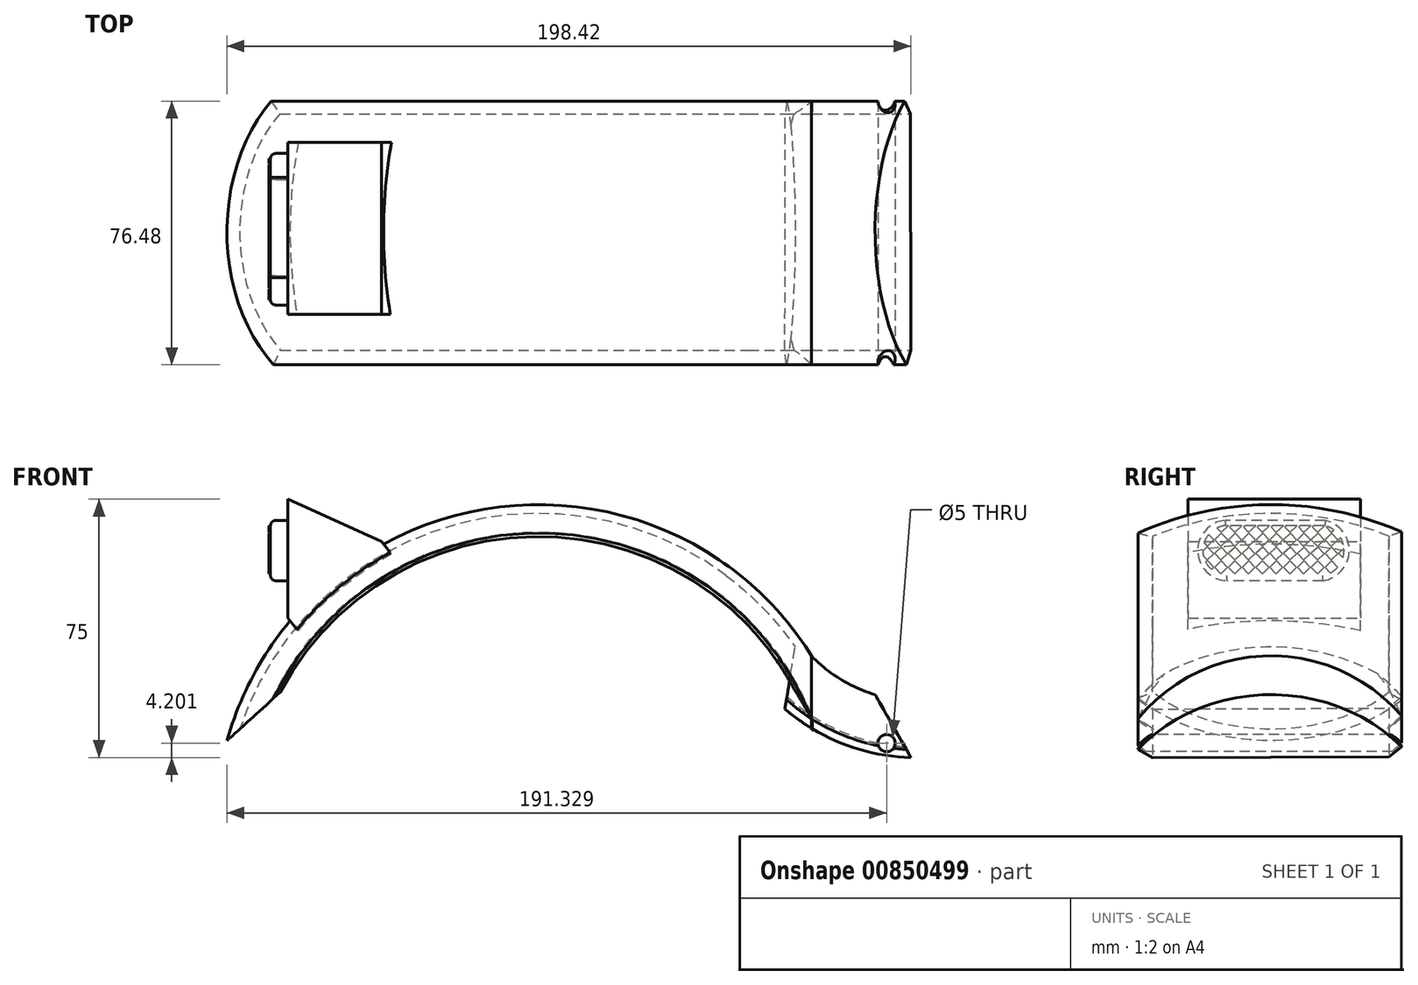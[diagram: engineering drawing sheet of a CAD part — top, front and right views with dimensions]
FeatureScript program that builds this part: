
annotation { "Feature Type Name" : "Feature", "Feature Type Description" : "" }
export const myFeature = defineFeature(function(context is Context, id is Id, definition is map)
    precondition{}
    {
        {
            var Q0;
            Q0=qCreatedBy(makeId("Front.planeOp"),FACE);
            var sketch = newSketch(context, id + "F0", { "sketchPlane" : qUnion([Q0])});
            skFitSpline(sketch, "E0", {"points": [v(68.37, 41.54) * mm, v(83.67, 28.77) * mm, v(119.21, 26.3) * mm], "startDerivative": vector(22.7, -35.07) * mm, "endDerivative": vector(68.28, -4.16) * mm});
            skLineSegment(sketch, "E1", {"start": v(68.5, 41.4) * mm, "end": v(68.47, 41.39) * mm});
            skArc(sketch, "E2.trimOffspring", {"start": v(68.5, 41.4) * mm, "mid": v(68.43, 41.47) * mm, "end": v(68.37, 41.54) * mm});
            skArc(sketch, "E3", {"start": v(68.5, 41.4) * mm, "mid": v(68.45, 41.44) * mm, "end": v(68.4, 41.48) * mm});
            skArc(sketch, "E4", {"start": v(68.37, 41.54) * mm, "mid": v(54.41, 56.97) * mm, "end": v(37.54, 69.12) * mm});
            skArc(sketch, "E5", {"start": v(37.54, 69.12) * mm, "mid": v(-52.48, 72.9) * mm, "end": v(-108.29, 2.17) * mm});
            skPoint(sketch, "E6.orphan", {"position": v(71.6, 37.23) * mm});
            skArc(sketch, "E7", {"start": v(68.4, 41.48) * mm, "mid": v(77.01, 32.62) * mm, "end": v(88.08, 27.14) * mm});
            skSolve(sketch);
        }
        {
            var Q0;
            Q0=qCreatedBy(makeId("Right.planeOp"),FACE);
            cPlane(context, id + "F1", {"entities" : qUnion([Q0]), "cplaneType" : CPlaneType.OFFSET, "offset" : 68 * mm, "width" : 150 * mm, "height" : 150 * mm});
        }
        {
            var Q0;
            Q0=qCreatedBy(id+"F1.planeOp",FACE);
            var sketch = newSketch(context, id + "F2", { "sketchPlane" : qUnion([Q0])});
            skArc(sketch, "E8", {"start": v(36.9, 15.62) * mm, "mid": v(-1.55, 32.94) * mm, "end": v(-39.57, 14.68) * mm});
            skArc(sketch, "E9.0", {"start": v(33.28, 12.17) * mm, "mid": v(-1.1, 27.94) * mm, "end": v(-35.37, 11.91) * mm});
            skLineSegment(sketch, "E10", {"start": v(-39.57, 14.68) * mm, "end": v(-35.37, 11.91) * mm});
            skLineSegment(sketch, "E11", {"start": v(36.9, 15.62) * mm, "end": v(33.28, 12.17) * mm});
            skLineSegment(sketch, "E12", {"start": v(-35.37, 11.91) * mm, "end": v(33.28, 12.17) * mm});
            skSolve(sketch);
        }
        {
            var Q0;
            Q0=makeQuery(id+"F2.imprint","IMPRINT",FACE,{"disambiguationData":[TD([[makeQuery(id+"F2.imprint","IMPRINT",EDGE,{"derivedFrom":sQuery(id+"F2.wireOp",EDGE,"E8")}),1.0]])]});
            var Q1;
            Q1=sQuery(id+"F0.wireOp",EDGE,"E4");
            var Q2;
            Q2=sQuery(id+"F0.wireOp",EDGE,"E5");
            sweep(context, id + "F3", {"profiles" : qUnion([Q0]), "path" : qUnion([Q1, Q2])});
        }
        {
            var Q0;
            Q0 = qSketchRegion(id + "F2", true);
            var Q1;
            Q1=sQuery(id+"F0.wireOp",EDGE,"E7");
            sweep(context, id + "F4", {"operationType" : NewBodyOperationType.ADD, "profiles" : qUnion([Q0]), "path" : qUnion([Q1])});
        }
        {
            var Q0;
            Q0=qCreatedBy(makeId("Front.planeOp"),FACE);
            var sketch = newSketch(context, id + "F5", { "sketchPlane" : qUnion([Q0])});
            skCircle(sketch, "E13", {"center": v(89.77, 7.6) * mm, "radius": 2.5 * mm});
            skSolve(sketch);
        }
        {
            var Q0;
            Q0 = qSketchRegion(id + "F5", true);
            extrude(context, id + "F6", {"entities" : qUnion([Q0]), "operationType" : NewBodyOperationType.REMOVE, "oppositeDirection" : true, "depth" : 100 * mm, "offsetDistance" : 25 * mm, "symmetric" : true});
        }
        {
            var Q0;
            Q0=qCreatedBy(makeId("Front.planeOp"),FACE);
            var sketch = newSketch(context, id + "F7", { "sketchPlane" : qUnion([Q0])});
            skLineSegment(sketch, "E14", {"start": v(-83.93, 78.4) * mm, "end": v(-83.93, 43.94) * mm});
            skLineSegment(sketch, "E15", {"start": v(-83.93, 78.4) * mm, "end": v(-56.75, 66.07) * mm});
            skLineSegment(sketch, "E16", {"start": v(-56.75, 66.07) * mm, "end": v(-83.93, 43.94) * mm});
            skSolve(sketch);
        }
        {
            var Q0;
            Q0=makeQuery(id+"F7.imprint","IMPRINT",FACE,{"disambiguationData":[TD([[makeQuery(id+"F7.imprint","IMPRINT",EDGE,{"derivedFrom":sQuery(id+"F7.wireOp",EDGE,"E14")}),1.0]])]});
            extrude(context, id + "F8", {"entities" : qUnion([Q0]), "operationType" : NewBodyOperationType.ADD, "depth" : 50 * mm, "offsetDistance" : 25 * mm, "symmetric" : true});
        }
        {
            var Q0;
            Q0=makeQuery(id+"F8.opExtrude","SWEPT_FACE",FACE,{"disambiguationData":[OSD([sQuery(id+"F7.wireOp",EDGE,"E16")])]});
            extrude(context, id + "F9", {"entities" : qUnion([Q0]), "operationType" : NewBodyOperationType.ADD, "endBound" : BoundingType.UP_TO_NEXT, "depth" : 25 * mm, "offsetDistance" : 25 * mm});
        }
        {
            var Q0;
            Q0=makeQuery(id+"F8.opExtrude","SWEPT_FACE",FACE,{"disambiguationData":[OSD([sQuery(id+"F7.wireOp",EDGE,"E14")])]});
            var sketch = newSketch(context, id + "F10", { "sketchPlane" : qUnion([Q0])});
            skLineSegment(sketch, "E17.bottom", {"start": v(-14.83, 72.23) * mm, "end": v(14.26, 72.23) * mm});
            skLineSegment(sketch, "E17.top", {"start": v(-14.17, 54.73) * mm, "end": v(13.78, 54.73) * mm});
            skArc(sketch, "E18", {"start": v(-14.83, 72.23) * mm, "mid": v(-21.73, 63.2) * mm, "end": v(-14.17, 54.73) * mm});
            skArc(sketch, "E19", {"start": v(13.78, 54.73) * mm, "mid": v(22.21, 63.26) * mm, "end": v(14.26, 72.23) * mm});
            skSolve(sketch);
        }
        {
            var Q0;
            Q0 = qSketchRegion(id + "F10", true);
            extrude(context, id + "F11", {"entities" : qUnion([Q0]), "depth" : 5 * mm, "offsetDistance" : 25 * mm});
        }
        {
            var Q0;
            Q0=makeQuery(id+"F11.opExtrude","CAP_EDGE",EDGE,{"disambiguationData":[OSD([sQuery(id+"F10.wireOp",EDGE,"E18")])],"isStart":false});
            var Q1;
            Q1=makeQuery(id+"F11.opExtrude","CAP_EDGE",EDGE,{"disambiguationData":[OSD([sQuery(id+"F10.wireOp",EDGE,"E17.bottom")])],"isStart":false});
            var Q2;
            Q2=makeQuery(id+"F11.opExtrude","CAP_FACE",FACE,{"disambiguationData":[OSD([sQuery(id+"F10.wireOp",EDGE,"E17.bottom"),sQuery(id+"F10.wireOp",EDGE,"E17.top"),sQuery(id+"F10.wireOp",EDGE,"E18"),sQuery(id+"F10.wireOp",EDGE,"E19")])],"isStart":false});
            fillet(context, id + "F12", {"entities" : qUnion([Q0, Q1, Q2]), "radius" : 1.5 * mm, "tangentPropagation" : true, "allowEdgeOverflow" : false});
        }
        {
            var Q0;
            Q0=makeQuery(id+"F11.opExtrude","CAP_FACE",FACE,{"disambiguationData":[OSD([sQuery(id+"F10.wireOp",EDGE,"E17.bottom"),sQuery(id+"F10.wireOp",EDGE,"E17.top"),sQuery(id+"F10.wireOp",EDGE,"E18"),sQuery(id+"F10.wireOp",EDGE,"E19")])],"isStart":false});
            var sketch = newSketch(context, id + "F13", { "sketchPlane" : qUnion([Q0])});
            skLineSegment(sketch, "E20", {"start": v(-14.65, 70.73) * mm, "end": v(-16.72, 68.56) * mm});
            skLineSegment(sketch, "E21", {"start": v(-16.72, 68.56) * mm, "end": v(-14.55, 66.49) * mm});
            skLineSegment(sketch, "E22", {"start": v(-14.55, 66.49) * mm, "end": v(-12.48, 68.66) * mm});
            skLineSegment(sketch, "E23", {"start": v(-12.48, 68.66) * mm, "end": v(-14.65, 70.73) * mm});
            skLineSegment(sketch, "E24.0", {"start": v(-16.01, 68.58) * mm, "end": v(-14.57, 67.2) * mm});
            skLineSegment(sketch, "E25.0", {"start": v(-14.63, 70.02) * mm, "end": v(-16.01, 68.58) * mm});
            skLineSegment(sketch, "E26.0", {"start": v(-13.19, 68.64) * mm, "end": v(-14.63, 70.02) * mm});
            skLineSegment(sketch, "E27.0", {"start": v(-14.57, 67.2) * mm, "end": v(-13.19, 68.64) * mm});
            skLineSegment(sketch, "E28.1.0.0", {"start": v(-10.65, 70.73) * mm, "end": v(-12.72, 68.56) * mm});
            skLineSegment(sketch, "E28.1.0.1", {"start": v(-10.63, 70.02) * mm, "end": v(-12.01, 68.58) * mm});
            skLineSegment(sketch, "E28.1.0.2", {"start": v(-9.19, 68.64) * mm, "end": v(-10.63, 70.02) * mm});
            skLineSegment(sketch, "E28.1.0.3", {"start": v(-8.48, 68.66) * mm, "end": v(-10.65, 70.73) * mm});
            skLineSegment(sketch, "E28.1.0.4", {"start": v(-10.55, 66.49) * mm, "end": v(-8.48, 68.66) * mm});
            skLineSegment(sketch, "E28.1.0.5", {"start": v(-10.57, 67.2) * mm, "end": v(-9.19, 68.64) * mm});
            skLineSegment(sketch, "E28.1.0.6", {"start": v(-12.01, 68.58) * mm, "end": v(-10.57, 67.2) * mm});
            skLineSegment(sketch, "E28.1.0.7", {"start": v(-12.72, 68.56) * mm, "end": v(-10.55, 66.49) * mm});
            skLineSegment(sketch, "E28.2.0.0", {"start": v(-6.65, 70.73) * mm, "end": v(-8.72, 68.56) * mm});
            skLineSegment(sketch, "E28.2.0.1", {"start": v(-6.63, 70.02) * mm, "end": v(-8.01, 68.58) * mm});
            skLineSegment(sketch, "E28.2.0.2", {"start": v(-5.19, 68.64) * mm, "end": v(-6.63, 70.02) * mm});
            skLineSegment(sketch, "E28.2.0.3", {"start": v(-4.48, 68.66) * mm, "end": v(-6.65, 70.73) * mm});
            skLineSegment(sketch, "E28.2.0.4", {"start": v(-6.55, 66.49) * mm, "end": v(-4.48, 68.66) * mm});
            skLineSegment(sketch, "E28.2.0.5", {"start": v(-6.57, 67.2) * mm, "end": v(-5.19, 68.64) * mm});
            skLineSegment(sketch, "E28.2.0.6", {"start": v(-8.01, 68.58) * mm, "end": v(-6.57, 67.2) * mm});
            skLineSegment(sketch, "E28.2.0.7", {"start": v(-8.72, 68.56) * mm, "end": v(-6.55, 66.49) * mm});
            skLineSegment(sketch, "E28.3.0.0", {"start": v(-2.65, 70.73) * mm, "end": v(-4.72, 68.56) * mm});
            skLineSegment(sketch, "E28.3.0.1", {"start": v(-2.63, 70.02) * mm, "end": v(-4.01, 68.58) * mm});
            skLineSegment(sketch, "E28.3.0.2", {"start": v(-1.19, 68.64) * mm, "end": v(-2.63, 70.02) * mm});
            skLineSegment(sketch, "E28.3.0.3", {"start": v(-0.48, 68.66) * mm, "end": v(-2.65, 70.73) * mm});
            skLineSegment(sketch, "E28.3.0.4", {"start": v(-2.55, 66.49) * mm, "end": v(-0.48, 68.66) * mm});
            skLineSegment(sketch, "E28.3.0.5", {"start": v(-2.57, 67.2) * mm, "end": v(-1.19, 68.64) * mm});
            skLineSegment(sketch, "E28.3.0.6", {"start": v(-4.01, 68.58) * mm, "end": v(-2.57, 67.2) * mm});
            skLineSegment(sketch, "E28.3.0.7", {"start": v(-4.72, 68.56) * mm, "end": v(-2.55, 66.49) * mm});
            skLineSegment(sketch, "E28.4.0.0", {"start": v(1.35, 70.73) * mm, "end": v(-0.72, 68.56) * mm});
            skLineSegment(sketch, "E28.4.0.1", {"start": v(1.37, 70.02) * mm, "end": v(-0.01, 68.58) * mm});
            skLineSegment(sketch, "E28.4.0.2", {"start": v(2.81, 68.64) * mm, "end": v(1.37, 70.02) * mm});
            skLineSegment(sketch, "E28.4.0.3", {"start": v(3.52, 68.66) * mm, "end": v(1.35, 70.73) * mm});
            skLineSegment(sketch, "E28.4.0.4", {"start": v(1.45, 66.49) * mm, "end": v(3.52, 68.66) * mm});
            skLineSegment(sketch, "E28.4.0.5", {"start": v(1.43, 67.2) * mm, "end": v(2.81, 68.64) * mm});
            skLineSegment(sketch, "E28.4.0.6", {"start": v(-0.01, 68.58) * mm, "end": v(1.43, 67.2) * mm});
            skLineSegment(sketch, "E28.4.0.7", {"start": v(-0.72, 68.56) * mm, "end": v(1.45, 66.49) * mm});
            skLineSegment(sketch, "E28.5.0.0", {"start": v(5.35, 70.73) * mm, "end": v(3.28, 68.56) * mm});
            skLineSegment(sketch, "E28.5.0.1", {"start": v(5.37, 70.02) * mm, "end": v(3.99, 68.58) * mm});
            skLineSegment(sketch, "E28.5.0.2", {"start": v(6.81, 68.64) * mm, "end": v(5.37, 70.02) * mm});
            skLineSegment(sketch, "E28.5.0.3", {"start": v(7.52, 68.66) * mm, "end": v(5.35, 70.73) * mm});
            skLineSegment(sketch, "E28.5.0.4", {"start": v(5.45, 66.49) * mm, "end": v(7.52, 68.66) * mm});
            skLineSegment(sketch, "E28.5.0.5", {"start": v(5.43, 67.2) * mm, "end": v(6.81, 68.64) * mm});
            skLineSegment(sketch, "E28.5.0.6", {"start": v(3.99, 68.58) * mm, "end": v(5.43, 67.2) * mm});
            skLineSegment(sketch, "E28.5.0.7", {"start": v(3.28, 68.56) * mm, "end": v(5.45, 66.49) * mm});
            skLineSegment(sketch, "E28.6.0.0", {"start": v(9.35, 70.73) * mm, "end": v(7.28, 68.56) * mm});
            skLineSegment(sketch, "E28.6.0.1", {"start": v(9.37, 70.02) * mm, "end": v(7.99, 68.58) * mm});
            skLineSegment(sketch, "E28.6.0.2", {"start": v(10.81, 68.64) * mm, "end": v(9.37, 70.02) * mm});
            skLineSegment(sketch, "E28.6.0.3", {"start": v(11.52, 68.66) * mm, "end": v(9.35, 70.73) * mm});
            skLineSegment(sketch, "E28.6.0.4", {"start": v(9.45, 66.49) * mm, "end": v(11.52, 68.66) * mm});
            skLineSegment(sketch, "E28.6.0.5", {"start": v(9.43, 67.2) * mm, "end": v(10.81, 68.64) * mm});
            skLineSegment(sketch, "E28.6.0.6", {"start": v(7.99, 68.58) * mm, "end": v(9.43, 67.2) * mm});
            skLineSegment(sketch, "E28.6.0.7", {"start": v(7.28, 68.56) * mm, "end": v(9.45, 66.49) * mm});
            skLineSegment(sketch, "E28.7.0.0", {"start": v(13.35, 70.73) * mm, "end": v(11.28, 68.56) * mm});
            skLineSegment(sketch, "E28.7.0.1", {"start": v(13.37, 70.02) * mm, "end": v(11.99, 68.58) * mm});
            skLineSegment(sketch, "E28.7.0.2", {"start": v(14.81, 68.64) * mm, "end": v(13.37, 70.02) * mm});
            skLineSegment(sketch, "E28.7.0.3", {"start": v(15.52, 68.66) * mm, "end": v(13.35, 70.73) * mm});
            skLineSegment(sketch, "E28.7.0.4", {"start": v(13.45, 66.49) * mm, "end": v(15.52, 68.66) * mm});
            skLineSegment(sketch, "E28.7.0.5", {"start": v(13.43, 67.2) * mm, "end": v(14.81, 68.64) * mm});
            skLineSegment(sketch, "E28.7.0.6", {"start": v(11.99, 68.58) * mm, "end": v(13.43, 67.2) * mm});
            skLineSegment(sketch, "E28.7.0.7", {"start": v(11.28, 68.56) * mm, "end": v(13.45, 66.49) * mm});
            skLineSegment(sketch, "E28.8.0.0", {"start": v(17.35, 70.73) * mm, "end": v(15.28, 68.56) * mm});
            skLineSegment(sketch, "E28.8.0.1", {"start": v(17.37, 70.02) * mm, "end": v(15.99, 68.58) * mm});
            skLineSegment(sketch, "E28.8.0.2", {"start": v(18.81, 68.64) * mm, "end": v(17.37, 70.02) * mm});
            skLineSegment(sketch, "E28.8.0.3", {"start": v(19.52, 68.66) * mm, "end": v(17.35, 70.73) * mm});
            skLineSegment(sketch, "E28.8.0.4", {"start": v(17.45, 66.49) * mm, "end": v(19.52, 68.66) * mm});
            skLineSegment(sketch, "E28.8.0.5", {"start": v(17.43, 67.2) * mm, "end": v(18.81, 68.64) * mm});
            skLineSegment(sketch, "E28.8.0.6", {"start": v(15.99, 68.58) * mm, "end": v(17.43, 67.2) * mm});
            skLineSegment(sketch, "E28.8.0.7", {"start": v(15.28, 68.56) * mm, "end": v(17.45, 66.49) * mm});
            skLineSegment(sketch, "E28.direction1", {"start": v(-16.72, 68.56) * mm, "end": v(-12.72, 68.56) * mm, "construction": true});
            skLineSegment(sketch, "E29.1.0.0", {"start": v(-18.65, 70.73) * mm, "end": v(-20.72, 68.56) * mm});
            skLineSegment(sketch, "E29.1.0.1", {"start": v(-16.48, 68.66) * mm, "end": v(-18.65, 70.73) * mm});
            skLineSegment(sketch, "E29.1.0.2", {"start": v(-18.55, 66.49) * mm, "end": v(-16.48, 68.66) * mm});
            skLineSegment(sketch, "E29.1.0.3", {"start": v(-17.19, 68.64) * mm, "end": v(-18.63, 70.02) * mm});
            skLineSegment(sketch, "E29.1.0.4", {"start": v(-18.63, 70.02) * mm, "end": v(-20.01, 68.58) * mm});
            skLineSegment(sketch, "E29.1.0.5", {"start": v(-20.01, 68.58) * mm, "end": v(-18.57, 67.2) * mm});
            skLineSegment(sketch, "E29.1.0.6", {"start": v(-18.57, 67.2) * mm, "end": v(-17.19, 68.64) * mm});
            skLineSegment(sketch, "E29.1.0.7", {"start": v(-20.72, 68.56) * mm, "end": v(-18.55, 66.49) * mm});
            skLineSegment(sketch, "E29.direction1", {"start": v(-16.72, 68.56) * mm, "end": v(-20.72, 68.56) * mm, "construction": true});
            skLineSegment(sketch, "E30.direction1", {"start": v(-18.63, 70.02) * mm, "end": v(-18.79, 67.03) * mm, "construction": true});
            skLineSegment(sketch, "E31.1.0.0", {"start": v(1.45, 63.2) * mm, "end": v(2.83, 64.64) * mm});
            skLineSegment(sketch, "E31.1.0.1", {"start": v(-9.17, 64.64) * mm, "end": v(-10.62, 66.02) * mm});
            skLineSegment(sketch, "E31.1.0.2", {"start": v(-8.46, 64.66) * mm, "end": v(-10.64, 66.73) * mm});
            skLineSegment(sketch, "E31.1.0.3", {"start": v(-6.64, 66.73) * mm, "end": v(-8.7, 64.56) * mm});
            skLineSegment(sketch, "E31.1.0.4", {"start": v(-2.62, 66.02) * mm, "end": v(-4, 64.58) * mm});
            skLineSegment(sketch, "E31.1.0.5", {"start": v(13.46, 62.49) * mm, "end": v(15.54, 64.66) * mm});
            skLineSegment(sketch, "E31.1.0.6", {"start": v(-2.55, 63.2) * mm, "end": v(-1.17, 64.64) * mm});
            skLineSegment(sketch, "E31.1.0.7", {"start": v(-14.54, 62.49) * mm, "end": v(-12.46, 64.66) * mm});
            skLineSegment(sketch, "E31.1.0.8", {"start": v(-16.46, 64.66) * mm, "end": v(-18.64, 66.73) * mm});
            skLineSegment(sketch, "E31.1.0.9", {"start": v(16, 64.58) * mm, "end": v(17.45, 63.2) * mm});
            skLineSegment(sketch, "E31.1.0.10", {"start": v(9.36, 66.73) * mm, "end": v(7.3, 64.56) * mm});
            skLineSegment(sketch, "E31.1.0.11", {"start": v(15.3, 64.56) * mm, "end": v(17.46, 62.49) * mm});
            skLineSegment(sketch, "E31.1.0.12", {"start": v(1.46, 62.49) * mm, "end": v(3.54, 64.66) * mm});
            skLineSegment(sketch, "E31.1.0.13", {"start": v(-8.7, 64.56) * mm, "end": v(-6.54, 62.49) * mm});
            skLineSegment(sketch, "E31.1.0.14", {"start": v(17.45, 63.2) * mm, "end": v(18.83, 64.64) * mm});
            skLineSegment(sketch, "E31.1.0.15", {"start": v(2.83, 64.64) * mm, "end": v(1.38, 66.02) * mm});
            skLineSegment(sketch, "E31.1.0.16", {"start": v(3.3, 64.56) * mm, "end": v(5.46, 62.49) * mm});
            skLineSegment(sketch, "E31.1.0.17", {"start": v(4, 64.58) * mm, "end": v(5.45, 63.2) * mm});
            skLineSegment(sketch, "E31.1.0.18", {"start": v(-20.7, 64.56) * mm, "end": v(-18.54, 62.49) * mm});
            skLineSegment(sketch, "E31.1.0.19", {"start": v(12, 64.58) * mm, "end": v(13.45, 63.2) * mm});
            skLineSegment(sketch, "E31.1.0.20", {"start": v(-10.55, 63.2) * mm, "end": v(-9.17, 64.64) * mm});
            skLineSegment(sketch, "E31.1.0.21", {"start": v(-12.7, 64.56) * mm, "end": v(-10.54, 62.49) * mm});
            skLineSegment(sketch, "E31.1.0.22", {"start": v(-8, 64.58) * mm, "end": v(-6.55, 63.2) * mm});
            skLineSegment(sketch, "E31.1.0.23", {"start": v(-14.64, 66.73) * mm, "end": v(-16.7, 64.56) * mm});
            skLineSegment(sketch, "E31.1.0.24", {"start": v(18.83, 64.64) * mm, "end": v(17.38, 66.02) * mm});
            skLineSegment(sketch, "E31.1.0.25", {"start": v(3.54, 64.66) * mm, "end": v(1.36, 66.73) * mm});
            skLineSegment(sketch, "E31.1.0.26", {"start": v(9.38, 66.02) * mm, "end": v(8, 64.58) * mm});
            skLineSegment(sketch, "E31.1.0.27", {"start": v(11.3, 64.56) * mm, "end": v(13.46, 62.49) * mm});
            skLineSegment(sketch, "E31.1.0.28", {"start": v(0, 64.58) * mm, "end": v(1.45, 63.2) * mm});
            skLineSegment(sketch, "E31.1.0.29", {"start": v(13.36, 66.73) * mm, "end": v(11.3, 64.56) * mm});
            skLineSegment(sketch, "E31.1.0.30", {"start": v(-10.64, 66.73) * mm, "end": v(-12.7, 64.56) * mm});
            skLineSegment(sketch, "E31.1.0.31", {"start": v(-0.46, 64.66) * mm, "end": v(-2.64, 66.73) * mm});
            skLineSegment(sketch, "E31.1.0.32", {"start": v(-12.46, 64.66) * mm, "end": v(-14.64, 66.73) * mm});
            skLineSegment(sketch, "E31.1.0.33", {"start": v(-6.55, 63.2) * mm, "end": v(-5.17, 64.64) * mm});
            skLineSegment(sketch, "E31.1.0.34", {"start": v(-18.64, 66.73) * mm, "end": v(-20.7, 64.56) * mm});
            skLineSegment(sketch, "E31.1.0.35", {"start": v(-18.55, 63.2) * mm, "end": v(-17.17, 64.64) * mm});
            skLineSegment(sketch, "E31.1.0.36", {"start": v(-1.17, 64.64) * mm, "end": v(-2.62, 66.02) * mm});
            skLineSegment(sketch, "E31.1.0.37", {"start": v(8, 64.58) * mm, "end": v(9.45, 63.2) * mm});
            skLineSegment(sketch, "E31.1.0.38", {"start": v(-4, 64.58) * mm, "end": v(-2.55, 63.2) * mm});
            skLineSegment(sketch, "E31.1.0.39", {"start": v(17.38, 66.02) * mm, "end": v(16, 64.58) * mm});
            skLineSegment(sketch, "E31.1.0.40", {"start": v(-16.7, 64.56) * mm, "end": v(-14.54, 62.49) * mm});
            skLineSegment(sketch, "E31.1.0.41", {"start": v(9.46, 62.49) * mm, "end": v(11.54, 64.66) * mm});
            skLineSegment(sketch, "E31.1.0.42", {"start": v(19.54, 64.66) * mm, "end": v(17.36, 66.73) * mm});
            skLineSegment(sketch, "E31.1.0.43", {"start": v(7.54, 64.66) * mm, "end": v(5.36, 66.73) * mm});
            skLineSegment(sketch, "E31.1.0.44", {"start": v(5.46, 62.49) * mm, "end": v(7.54, 64.66) * mm});
            skLineSegment(sketch, "E31.1.0.45", {"start": v(13.45, 63.2) * mm, "end": v(14.83, 64.64) * mm});
            skLineSegment(sketch, "E31.1.0.46", {"start": v(11.54, 64.66) * mm, "end": v(9.36, 66.73) * mm});
            skLineSegment(sketch, "E31.1.0.47", {"start": v(-20, 64.58) * mm, "end": v(-18.55, 63.2) * mm});
            skLineSegment(sketch, "E31.1.0.48", {"start": v(-6.54, 62.49) * mm, "end": v(-4.46, 64.66) * mm});
            skLineSegment(sketch, "E31.1.0.49", {"start": v(10.83, 64.64) * mm, "end": v(9.38, 66.02) * mm});
            skLineSegment(sketch, "E31.1.0.50", {"start": v(9.45, 63.2) * mm, "end": v(10.83, 64.64) * mm});
            skLineSegment(sketch, "E31.1.0.51", {"start": v(7.3, 64.56) * mm, "end": v(9.46, 62.49) * mm});
            skLineSegment(sketch, "E31.1.0.52", {"start": v(-2.54, 62.49) * mm, "end": v(-0.46, 64.66) * mm});
            skLineSegment(sketch, "E31.1.0.53", {"start": v(-10.54, 62.49) * mm, "end": v(-8.46, 64.66) * mm});
            skLineSegment(sketch, "E31.1.0.54", {"start": v(-10.62, 66.02) * mm, "end": v(-12, 64.58) * mm});
            skLineSegment(sketch, "E31.1.0.55", {"start": v(1.38, 66.02) * mm, "end": v(0, 64.58) * mm});
            skLineSegment(sketch, "E31.1.0.56", {"start": v(-0.7, 64.56) * mm, "end": v(1.46, 62.49) * mm});
            skLineSegment(sketch, "E31.1.0.57", {"start": v(5.38, 66.02) * mm, "end": v(4, 64.58) * mm});
            skLineSegment(sketch, "E31.1.0.58", {"start": v(17.36, 66.73) * mm, "end": v(15.3, 64.56) * mm});
            skLineSegment(sketch, "E31.1.0.59", {"start": v(13.38, 66.02) * mm, "end": v(12, 64.58) * mm});
            skLineSegment(sketch, "E31.1.0.60", {"start": v(-18.54, 62.49) * mm, "end": v(-16.46, 64.66) * mm});
            skLineSegment(sketch, "E31.1.0.61", {"start": v(14.83, 64.64) * mm, "end": v(13.38, 66.02) * mm});
            skLineSegment(sketch, "E31.1.0.62", {"start": v(-6.62, 66.02) * mm, "end": v(-8, 64.58) * mm});
            skLineSegment(sketch, "E31.1.0.63", {"start": v(17.46, 62.49) * mm, "end": v(19.54, 64.66) * mm});
            skLineSegment(sketch, "E31.1.0.64", {"start": v(-12, 64.58) * mm, "end": v(-10.55, 63.2) * mm});
            skLineSegment(sketch, "E31.1.0.65", {"start": v(5.36, 66.73) * mm, "end": v(3.3, 64.56) * mm});
            skLineSegment(sketch, "E31.1.0.66", {"start": v(1.36, 66.73) * mm, "end": v(-0.7, 64.56) * mm});
            skLineSegment(sketch, "E31.1.0.67", {"start": v(-18.62, 66.02) * mm, "end": v(-20, 64.58) * mm});
            skLineSegment(sketch, "E31.1.0.68", {"start": v(-14.55, 63.2) * mm, "end": v(-13.17, 64.64) * mm});
            skLineSegment(sketch, "E31.1.0.69", {"start": v(-4.7, 64.56) * mm, "end": v(-2.54, 62.49) * mm});
            skLineSegment(sketch, "E31.1.0.70", {"start": v(5.45, 63.2) * mm, "end": v(6.83, 64.64) * mm});
            skLineSegment(sketch, "E31.1.0.71", {"start": v(-4.46, 64.66) * mm, "end": v(-6.64, 66.73) * mm});
            skLineSegment(sketch, "E31.1.0.72", {"start": v(-5.17, 64.64) * mm, "end": v(-6.62, 66.02) * mm});
            skLineSegment(sketch, "E31.1.0.73", {"start": v(-13.17, 64.64) * mm, "end": v(-14.62, 66.02) * mm});
            skLineSegment(sketch, "E31.1.0.74", {"start": v(6.83, 64.64) * mm, "end": v(5.38, 66.02) * mm});
            skLineSegment(sketch, "E31.1.0.75", {"start": v(-14.62, 66.02) * mm, "end": v(-16, 64.58) * mm});
            skLineSegment(sketch, "E31.1.0.76", {"start": v(-17.17, 64.64) * mm, "end": v(-18.62, 66.02) * mm});
            skLineSegment(sketch, "E31.1.0.77", {"start": v(-2.64, 66.73) * mm, "end": v(-4.7, 64.56) * mm});
            skLineSegment(sketch, "E31.1.0.78", {"start": v(15.54, 64.66) * mm, "end": v(13.36, 66.73) * mm});
            skLineSegment(sketch, "E31.1.0.79", {"start": v(-16, 64.58) * mm, "end": v(-14.55, 63.2) * mm});
            skLineSegment(sketch, "E31.2.0.0", {"start": v(1.46, 59.2) * mm, "end": v(2.84, 60.64) * mm});
            skLineSegment(sketch, "E31.2.0.1", {"start": v(-9.16, 60.64) * mm, "end": v(-10.6, 62.02) * mm});
            skLineSegment(sketch, "E31.2.0.2", {"start": v(-8.45, 60.66) * mm, "end": v(-10.62, 62.73) * mm});
            skLineSegment(sketch, "E31.2.0.3", {"start": v(-6.62, 62.73) * mm, "end": v(-8.7, 60.56) * mm});
            skLineSegment(sketch, "E31.2.0.4", {"start": v(-2.6, 62.02) * mm, "end": v(-3.98, 60.58) * mm});
            skLineSegment(sketch, "E31.2.0.5", {"start": v(13.48, 58.49) * mm, "end": v(15.55, 60.66) * mm});
            skLineSegment(sketch, "E31.2.0.6", {"start": v(-2.54, 59.2) * mm, "end": v(-1.16, 60.64) * mm});
            skLineSegment(sketch, "E31.2.0.7", {"start": v(-14.52, 58.49) * mm, "end": v(-12.45, 60.66) * mm});
            skLineSegment(sketch, "E31.2.0.8", {"start": v(-16.45, 60.66) * mm, "end": v(-18.62, 62.73) * mm});
            skLineSegment(sketch, "E31.2.0.9", {"start": v(16.02, 60.58) * mm, "end": v(17.46, 59.2) * mm});
            skLineSegment(sketch, "E31.2.0.10", {"start": v(9.38, 62.73) * mm, "end": v(7.3, 60.56) * mm});
            skLineSegment(sketch, "E31.2.0.11", {"start": v(15.3, 60.56) * mm, "end": v(17.48, 58.49) * mm});
            skLineSegment(sketch, "E31.2.0.12", {"start": v(1.48, 58.49) * mm, "end": v(3.55, 60.66) * mm});
            skLineSegment(sketch, "E31.2.0.13", {"start": v(-8.7, 60.56) * mm, "end": v(-6.52, 58.49) * mm});
            skLineSegment(sketch, "E31.2.0.14", {"start": v(17.46, 59.2) * mm, "end": v(18.84, 60.64) * mm});
            skLineSegment(sketch, "E31.2.0.15", {"start": v(2.84, 60.64) * mm, "end": v(1.4, 62.02) * mm});
            skLineSegment(sketch, "E31.2.0.16", {"start": v(3.3, 60.56) * mm, "end": v(5.48, 58.49) * mm});
            skLineSegment(sketch, "E31.2.0.17", {"start": v(4.02, 60.58) * mm, "end": v(5.46, 59.2) * mm});
            skLineSegment(sketch, "E31.2.0.18", {"start": v(-20.7, 60.56) * mm, "end": v(-18.52, 58.49) * mm});
            skLineSegment(sketch, "E31.2.0.19", {"start": v(12.02, 60.58) * mm, "end": v(13.46, 59.2) * mm});
            skLineSegment(sketch, "E31.2.0.20", {"start": v(-10.54, 59.2) * mm, "end": v(-9.16, 60.64) * mm});
            skLineSegment(sketch, "E31.2.0.21", {"start": v(-12.7, 60.56) * mm, "end": v(-10.52, 58.49) * mm});
            skLineSegment(sketch, "E31.2.0.22", {"start": v(-7.98, 60.58) * mm, "end": v(-6.54, 59.2) * mm});
            skLineSegment(sketch, "E31.2.0.23", {"start": v(-14.62, 62.73) * mm, "end": v(-16.7, 60.56) * mm});
            skLineSegment(sketch, "E31.2.0.24", {"start": v(18.84, 60.64) * mm, "end": v(17.4, 62.02) * mm});
            skLineSegment(sketch, "E31.2.0.25", {"start": v(3.55, 60.66) * mm, "end": v(1.38, 62.73) * mm});
            skLineSegment(sketch, "E31.2.0.26", {"start": v(9.4, 62.02) * mm, "end": v(8.02, 60.58) * mm});
            skLineSegment(sketch, "E31.2.0.27", {"start": v(11.3, 60.56) * mm, "end": v(13.48, 58.49) * mm});
            skLineSegment(sketch, "E31.2.0.28", {"start": v(0.02, 60.58) * mm, "end": v(1.46, 59.2) * mm});
            skLineSegment(sketch, "E31.2.0.29", {"start": v(13.38, 62.73) * mm, "end": v(11.3, 60.56) * mm});
            skLineSegment(sketch, "E31.2.0.30", {"start": v(-10.62, 62.73) * mm, "end": v(-12.7, 60.56) * mm});
            skLineSegment(sketch, "E31.2.0.31", {"start": v(-0.45, 60.66) * mm, "end": v(-2.62, 62.73) * mm});
            skLineSegment(sketch, "E31.2.0.32", {"start": v(-12.45, 60.66) * mm, "end": v(-14.62, 62.73) * mm});
            skLineSegment(sketch, "E31.2.0.33", {"start": v(-6.54, 59.2) * mm, "end": v(-5.16, 60.64) * mm});
            skLineSegment(sketch, "E31.2.0.34", {"start": v(-18.62, 62.73) * mm, "end": v(-20.7, 60.56) * mm});
            skLineSegment(sketch, "E31.2.0.35", {"start": v(-18.54, 59.2) * mm, "end": v(-17.16, 60.64) * mm});
            skLineSegment(sketch, "E31.2.0.36", {"start": v(-1.16, 60.64) * mm, "end": v(-2.6, 62.02) * mm});
            skLineSegment(sketch, "E31.2.0.37", {"start": v(8.02, 60.58) * mm, "end": v(9.46, 59.2) * mm});
            skLineSegment(sketch, "E31.2.0.38", {"start": v(-3.98, 60.58) * mm, "end": v(-2.54, 59.2) * mm});
            skLineSegment(sketch, "E31.2.0.39", {"start": v(17.4, 62.02) * mm, "end": v(16.02, 60.58) * mm});
            skLineSegment(sketch, "E31.2.0.40", {"start": v(-16.7, 60.56) * mm, "end": v(-14.52, 58.49) * mm});
            skLineSegment(sketch, "E31.2.0.41", {"start": v(9.48, 58.49) * mm, "end": v(11.55, 60.66) * mm});
            skLineSegment(sketch, "E31.2.0.42", {"start": v(19.55, 60.66) * mm, "end": v(17.38, 62.73) * mm});
            skLineSegment(sketch, "E31.2.0.43", {"start": v(7.55, 60.66) * mm, "end": v(5.38, 62.73) * mm});
            skLineSegment(sketch, "E31.2.0.44", {"start": v(5.48, 58.49) * mm, "end": v(7.55, 60.66) * mm});
            skLineSegment(sketch, "E31.2.0.45", {"start": v(13.46, 59.2) * mm, "end": v(14.84, 60.64) * mm});
            skLineSegment(sketch, "E31.2.0.46", {"start": v(11.55, 60.66) * mm, "end": v(9.38, 62.73) * mm});
            skLineSegment(sketch, "E31.2.0.47", {"start": v(-19.98, 60.58) * mm, "end": v(-18.54, 59.2) * mm});
            skLineSegment(sketch, "E31.2.0.48", {"start": v(-6.52, 58.49) * mm, "end": v(-4.45, 60.66) * mm});
            skLineSegment(sketch, "E31.2.0.49", {"start": v(10.84, 60.64) * mm, "end": v(9.4, 62.02) * mm});
            skLineSegment(sketch, "E31.2.0.50", {"start": v(9.46, 59.2) * mm, "end": v(10.84, 60.64) * mm});
            skLineSegment(sketch, "E31.2.0.51", {"start": v(7.3, 60.56) * mm, "end": v(9.48, 58.49) * mm});
            skLineSegment(sketch, "E31.2.0.52", {"start": v(-2.52, 58.49) * mm, "end": v(-0.45, 60.66) * mm});
            skLineSegment(sketch, "E31.2.0.53", {"start": v(-10.52, 58.49) * mm, "end": v(-8.45, 60.66) * mm});
            skLineSegment(sketch, "E31.2.0.54", {"start": v(-10.6, 62.02) * mm, "end": v(-11.98, 60.58) * mm});
            skLineSegment(sketch, "E31.2.0.55", {"start": v(1.4, 62.02) * mm, "end": v(0.02, 60.58) * mm});
            skLineSegment(sketch, "E31.2.0.56", {"start": v(-0.7, 60.56) * mm, "end": v(1.48, 58.49) * mm});
            skLineSegment(sketch, "E31.2.0.57", {"start": v(5.4, 62.02) * mm, "end": v(4.02, 60.58) * mm});
            skLineSegment(sketch, "E31.2.0.58", {"start": v(17.38, 62.73) * mm, "end": v(15.3, 60.56) * mm});
            skLineSegment(sketch, "E31.2.0.59", {"start": v(13.4, 62.02) * mm, "end": v(12.02, 60.58) * mm});
            skLineSegment(sketch, "E31.2.0.60", {"start": v(-18.52, 58.49) * mm, "end": v(-16.45, 60.66) * mm});
            skLineSegment(sketch, "E31.2.0.61", {"start": v(14.84, 60.64) * mm, "end": v(13.4, 62.02) * mm});
            skLineSegment(sketch, "E31.2.0.62", {"start": v(-6.6, 62.02) * mm, "end": v(-7.98, 60.58) * mm});
            skLineSegment(sketch, "E31.2.0.63", {"start": v(17.48, 58.49) * mm, "end": v(19.55, 60.66) * mm});
            skLineSegment(sketch, "E31.2.0.64", {"start": v(-11.98, 60.58) * mm, "end": v(-10.54, 59.2) * mm});
            skLineSegment(sketch, "E31.2.0.65", {"start": v(5.38, 62.73) * mm, "end": v(3.3, 60.56) * mm});
            skLineSegment(sketch, "E31.2.0.66", {"start": v(1.38, 62.73) * mm, "end": v(-0.7, 60.56) * mm});
            skLineSegment(sketch, "E31.2.0.67", {"start": v(-18.6, 62.02) * mm, "end": v(-19.98, 60.58) * mm});
            skLineSegment(sketch, "E31.2.0.68", {"start": v(-14.54, 59.2) * mm, "end": v(-13.16, 60.64) * mm});
            skLineSegment(sketch, "E31.2.0.69", {"start": v(-4.7, 60.56) * mm, "end": v(-2.52, 58.49) * mm});
            skLineSegment(sketch, "E31.2.0.70", {"start": v(5.46, 59.2) * mm, "end": v(6.84, 60.64) * mm});
            skLineSegment(sketch, "E31.2.0.71", {"start": v(-4.45, 60.66) * mm, "end": v(-6.62, 62.73) * mm});
            skLineSegment(sketch, "E31.2.0.72", {"start": v(-5.16, 60.64) * mm, "end": v(-6.6, 62.02) * mm});
            skLineSegment(sketch, "E31.2.0.73", {"start": v(-13.16, 60.64) * mm, "end": v(-14.6, 62.02) * mm});
            skLineSegment(sketch, "E31.2.0.74", {"start": v(6.84, 60.64) * mm, "end": v(5.4, 62.02) * mm});
            skLineSegment(sketch, "E31.2.0.75", {"start": v(-14.6, 62.02) * mm, "end": v(-15.98, 60.58) * mm});
            skLineSegment(sketch, "E31.2.0.76", {"start": v(-17.16, 60.64) * mm, "end": v(-18.6, 62.02) * mm});
            skLineSegment(sketch, "E31.2.0.77", {"start": v(-2.62, 62.73) * mm, "end": v(-4.7, 60.56) * mm});
            skLineSegment(sketch, "E31.2.0.78", {"start": v(15.55, 60.66) * mm, "end": v(13.38, 62.73) * mm});
            skLineSegment(sketch, "E31.2.0.79", {"start": v(-15.98, 60.58) * mm, "end": v(-14.54, 59.2) * mm});
            skLineSegment(sketch, "E31.3.0.0", {"start": v(1.48, 55.2) * mm, "end": v(2.86, 56.64) * mm});
            skLineSegment(sketch, "E31.3.0.1", {"start": v(-9.14, 56.64) * mm, "end": v(-10.59, 58.02) * mm});
            skLineSegment(sketch, "E31.3.0.2", {"start": v(-8.43, 56.66) * mm, "end": v(-10.6, 58.73) * mm});
            skLineSegment(sketch, "E31.3.0.3", {"start": v(-6.6, 58.73) * mm, "end": v(-8.68, 56.56) * mm});
            skLineSegment(sketch, "E31.3.0.4", {"start": v(-2.59, 58.02) * mm, "end": v(-3.97, 56.58) * mm});
            skLineSegment(sketch, "E31.3.0.5", {"start": v(13.5, 54.49) * mm, "end": v(15.57, 56.66) * mm});
            skLineSegment(sketch, "E31.3.0.6", {"start": v(-2.52, 55.2) * mm, "end": v(-1.14, 56.64) * mm});
            skLineSegment(sketch, "E31.3.0.7", {"start": v(-14.5, 54.49) * mm, "end": v(-12.43, 56.66) * mm});
            skLineSegment(sketch, "E31.3.0.8", {"start": v(-16.43, 56.66) * mm, "end": v(-18.6, 58.73) * mm});
            skLineSegment(sketch, "E31.3.0.9", {"start": v(16.03, 56.58) * mm, "end": v(17.48, 55.2) * mm});
            skLineSegment(sketch, "E31.3.0.10", {"start": v(9.4, 58.73) * mm, "end": v(7.32, 56.56) * mm});
            skLineSegment(sketch, "E31.3.0.11", {"start": v(15.32, 56.56) * mm, "end": v(17.5, 54.49) * mm});
            skLineSegment(sketch, "E31.3.0.12", {"start": v(1.5, 54.49) * mm, "end": v(3.57, 56.66) * mm});
            skLineSegment(sketch, "E31.3.0.13", {"start": v(-8.68, 56.56) * mm, "end": v(-6.5, 54.49) * mm});
            skLineSegment(sketch, "E31.3.0.14", {"start": v(17.48, 55.2) * mm, "end": v(18.86, 56.64) * mm});
            skLineSegment(sketch, "E31.3.0.15", {"start": v(2.86, 56.64) * mm, "end": v(1.41, 58.02) * mm});
            skLineSegment(sketch, "E31.3.0.16", {"start": v(3.32, 56.56) * mm, "end": v(5.5, 54.49) * mm});
            skLineSegment(sketch, "E31.3.0.17", {"start": v(4.03, 56.58) * mm, "end": v(5.48, 55.2) * mm});
            skLineSegment(sketch, "E31.3.0.18", {"start": v(-20.68, 56.56) * mm, "end": v(-18.5, 54.49) * mm});
            skLineSegment(sketch, "E31.3.0.19", {"start": v(12.03, 56.58) * mm, "end": v(13.48, 55.2) * mm});
            skLineSegment(sketch, "E31.3.0.20", {"start": v(-10.52, 55.2) * mm, "end": v(-9.14, 56.64) * mm});
            skLineSegment(sketch, "E31.3.0.21", {"start": v(-12.68, 56.56) * mm, "end": v(-10.5, 54.49) * mm});
            skLineSegment(sketch, "E31.3.0.22", {"start": v(-7.97, 56.58) * mm, "end": v(-6.52, 55.2) * mm});
            skLineSegment(sketch, "E31.3.0.23", {"start": v(-14.6, 58.73) * mm, "end": v(-16.68, 56.56) * mm});
            skLineSegment(sketch, "E31.3.0.24", {"start": v(18.86, 56.64) * mm, "end": v(17.41, 58.02) * mm});
            skLineSegment(sketch, "E31.3.0.25", {"start": v(3.57, 56.66) * mm, "end": v(1.4, 58.73) * mm});
            skLineSegment(sketch, "E31.3.0.26", {"start": v(9.41, 58.02) * mm, "end": v(8.03, 56.58) * mm});
            skLineSegment(sketch, "E31.3.0.27", {"start": v(11.32, 56.56) * mm, "end": v(13.5, 54.49) * mm});
            skLineSegment(sketch, "E31.3.0.28", {"start": v(0.03, 56.58) * mm, "end": v(1.48, 55.2) * mm});
            skLineSegment(sketch, "E31.3.0.29", {"start": v(13.4, 58.73) * mm, "end": v(11.32, 56.56) * mm});
            skLineSegment(sketch, "E31.3.0.30", {"start": v(-10.6, 58.73) * mm, "end": v(-12.68, 56.56) * mm});
            skLineSegment(sketch, "E31.3.0.31", {"start": v(-0.43, 56.66) * mm, "end": v(-2.6, 58.73) * mm});
            skLineSegment(sketch, "E31.3.0.32", {"start": v(-12.43, 56.66) * mm, "end": v(-14.6, 58.73) * mm});
            skLineSegment(sketch, "E31.3.0.33", {"start": v(-6.52, 55.2) * mm, "end": v(-5.14, 56.64) * mm});
            skLineSegment(sketch, "E31.3.0.34", {"start": v(-18.6, 58.73) * mm, "end": v(-20.68, 56.56) * mm});
            skLineSegment(sketch, "E31.3.0.35", {"start": v(-18.52, 55.2) * mm, "end": v(-17.14, 56.64) * mm});
            skLineSegment(sketch, "E31.3.0.36", {"start": v(-1.14, 56.64) * mm, "end": v(-2.59, 58.02) * mm});
            skLineSegment(sketch, "E31.3.0.37", {"start": v(8.03, 56.58) * mm, "end": v(9.48, 55.2) * mm});
            skLineSegment(sketch, "E31.3.0.38", {"start": v(-3.97, 56.58) * mm, "end": v(-2.52, 55.2) * mm});
            skLineSegment(sketch, "E31.3.0.39", {"start": v(17.41, 58.02) * mm, "end": v(16.03, 56.58) * mm});
            skLineSegment(sketch, "E31.3.0.40", {"start": v(-16.68, 56.56) * mm, "end": v(-14.5, 54.49) * mm});
            skLineSegment(sketch, "E31.3.0.41", {"start": v(9.5, 54.49) * mm, "end": v(11.57, 56.66) * mm});
            skLineSegment(sketch, "E31.3.0.42", {"start": v(19.57, 56.66) * mm, "end": v(17.4, 58.73) * mm});
            skLineSegment(sketch, "E31.3.0.43", {"start": v(7.57, 56.66) * mm, "end": v(5.4, 58.73) * mm});
            skLineSegment(sketch, "E31.3.0.44", {"start": v(5.5, 54.49) * mm, "end": v(7.57, 56.66) * mm});
            skLineSegment(sketch, "E31.3.0.45", {"start": v(13.48, 55.2) * mm, "end": v(14.86, 56.64) * mm});
            skLineSegment(sketch, "E31.3.0.46", {"start": v(11.57, 56.66) * mm, "end": v(9.4, 58.73) * mm});
            skLineSegment(sketch, "E31.3.0.47", {"start": v(-19.97, 56.58) * mm, "end": v(-18.52, 55.2) * mm});
            skLineSegment(sketch, "E31.3.0.48", {"start": v(-6.5, 54.49) * mm, "end": v(-4.43, 56.66) * mm});
            skLineSegment(sketch, "E31.3.0.49", {"start": v(10.86, 56.64) * mm, "end": v(9.41, 58.02) * mm});
            skLineSegment(sketch, "E31.3.0.50", {"start": v(9.48, 55.2) * mm, "end": v(10.86, 56.64) * mm});
            skLineSegment(sketch, "E31.3.0.51", {"start": v(7.32, 56.56) * mm, "end": v(9.5, 54.49) * mm});
            skLineSegment(sketch, "E31.3.0.52", {"start": v(-2.5, 54.49) * mm, "end": v(-0.43, 56.66) * mm});
            skLineSegment(sketch, "E31.3.0.53", {"start": v(-10.5, 54.49) * mm, "end": v(-8.43, 56.66) * mm});
            skLineSegment(sketch, "E31.3.0.54", {"start": v(-10.59, 58.02) * mm, "end": v(-11.97, 56.58) * mm});
            skLineSegment(sketch, "E31.3.0.55", {"start": v(1.41, 58.02) * mm, "end": v(0.03, 56.58) * mm});
            skLineSegment(sketch, "E31.3.0.56", {"start": v(-0.68, 56.56) * mm, "end": v(1.5, 54.49) * mm});
            skLineSegment(sketch, "E31.3.0.57", {"start": v(5.41, 58.02) * mm, "end": v(4.03, 56.58) * mm});
            skLineSegment(sketch, "E31.3.0.58", {"start": v(17.4, 58.73) * mm, "end": v(15.32, 56.56) * mm});
            skLineSegment(sketch, "E31.3.0.59", {"start": v(13.41, 58.02) * mm, "end": v(12.03, 56.58) * mm});
            skLineSegment(sketch, "E31.3.0.60", {"start": v(-18.5, 54.49) * mm, "end": v(-16.43, 56.66) * mm});
            skLineSegment(sketch, "E31.3.0.61", {"start": v(14.86, 56.64) * mm, "end": v(13.41, 58.02) * mm});
            skLineSegment(sketch, "E31.3.0.62", {"start": v(-6.59, 58.02) * mm, "end": v(-7.97, 56.58) * mm});
            skLineSegment(sketch, "E31.3.0.63", {"start": v(17.5, 54.49) * mm, "end": v(19.57, 56.66) * mm});
            skLineSegment(sketch, "E31.3.0.64", {"start": v(-11.97, 56.58) * mm, "end": v(-10.52, 55.2) * mm});
            skLineSegment(sketch, "E31.3.0.65", {"start": v(5.4, 58.73) * mm, "end": v(3.32, 56.56) * mm});
            skLineSegment(sketch, "E31.3.0.66", {"start": v(1.4, 58.73) * mm, "end": v(-0.68, 56.56) * mm});
            skLineSegment(sketch, "E31.3.0.67", {"start": v(-18.59, 58.02) * mm, "end": v(-19.97, 56.58) * mm});
            skLineSegment(sketch, "E31.3.0.68", {"start": v(-14.52, 55.2) * mm, "end": v(-13.14, 56.64) * mm});
            skLineSegment(sketch, "E31.3.0.69", {"start": v(-4.68, 56.56) * mm, "end": v(-2.5, 54.49) * mm});
            skLineSegment(sketch, "E31.3.0.70", {"start": v(5.48, 55.2) * mm, "end": v(6.86, 56.64) * mm});
            skLineSegment(sketch, "E31.3.0.71", {"start": v(-4.43, 56.66) * mm, "end": v(-6.6, 58.73) * mm});
            skLineSegment(sketch, "E31.3.0.72", {"start": v(-5.14, 56.64) * mm, "end": v(-6.59, 58.02) * mm});
            skLineSegment(sketch, "E31.3.0.73", {"start": v(-13.14, 56.64) * mm, "end": v(-14.59, 58.02) * mm});
            skLineSegment(sketch, "E31.3.0.74", {"start": v(6.86, 56.64) * mm, "end": v(5.41, 58.02) * mm});
            skLineSegment(sketch, "E31.3.0.75", {"start": v(-14.59, 58.02) * mm, "end": v(-15.97, 56.58) * mm});
            skLineSegment(sketch, "E31.3.0.76", {"start": v(-17.14, 56.64) * mm, "end": v(-18.59, 58.02) * mm});
            skLineSegment(sketch, "E31.3.0.77", {"start": v(-2.6, 58.73) * mm, "end": v(-4.68, 56.56) * mm});
            skLineSegment(sketch, "E31.3.0.78", {"start": v(15.57, 56.66) * mm, "end": v(13.4, 58.73) * mm});
            skLineSegment(sketch, "E31.3.0.79", {"start": v(-15.97, 56.58) * mm, "end": v(-14.52, 55.2) * mm});
            skLineSegment(sketch, "E31.direction1", {"start": v(-20.72, 68.56) * mm, "end": v(-20.7, 64.56) * mm, "construction": true});
            skLineSegment(sketch, "E32.0.9.0", {"start": v(21.35, 70.73) * mm, "end": v(19.28, 68.56) * mm});
            skLineSegment(sketch, "E32.3.9.0", {"start": v(21.37, 70.02) * mm, "end": v(19.99, 68.58) * mm});
            skLineSegment(sketch, "E32.6.9.0", {"start": v(22.81, 68.64) * mm, "end": v(21.37, 70.02) * mm});
            skLineSegment(sketch, "E32.9.9.0", {"start": v(23.52, 68.66) * mm, "end": v(21.35, 70.73) * mm});
            skLineSegment(sketch, "E32.12.9.0", {"start": v(21.45, 66.49) * mm, "end": v(23.52, 68.66) * mm});
            skLineSegment(sketch, "E32.15.9.0", {"start": v(21.43, 67.2) * mm, "end": v(22.81, 68.64) * mm});
            skLineSegment(sketch, "E32.18.9.0", {"start": v(19.99, 68.58) * mm, "end": v(21.43, 67.2) * mm});
            skLineSegment(sketch, "E32.21.9.0", {"start": v(19.28, 68.56) * mm, "end": v(21.45, 66.49) * mm});
            skLineSegment(sketch, "E33.1.0.0", {"start": v(21.42, 66.1) * mm, "end": v(20.04, 64.65) * mm});
            skLineSegment(sketch, "E33.1.0.1", {"start": v(21.48, 63.27) * mm, "end": v(22.86, 64.71) * mm});
            skLineSegment(sketch, "E33.1.0.2", {"start": v(23.57, 64.73) * mm, "end": v(21.4, 66.8) * mm});
            skLineSegment(sketch, "E33.1.0.3", {"start": v(22.86, 64.71) * mm, "end": v(21.42, 66.1) * mm});
            skLineSegment(sketch, "E33.1.0.4", {"start": v(21.5, 62.56) * mm, "end": v(23.57, 64.73) * mm});
            skLineSegment(sketch, "E33.1.0.5", {"start": v(19.33, 64.63) * mm, "end": v(21.5, 62.56) * mm});
            skLineSegment(sketch, "E33.1.0.6", {"start": v(20.04, 64.65) * mm, "end": v(21.48, 63.27) * mm});
            skLineSegment(sketch, "E33.1.0.7", {"start": v(21.4, 66.8) * mm, "end": v(19.33, 64.63) * mm});
            skLineSegment(sketch, "E33.2.0.0", {"start": v(21.47, 62.17) * mm, "end": v(20.09, 60.72) * mm});
            skLineSegment(sketch, "E33.2.0.1", {"start": v(21.53, 59.34) * mm, "end": v(22.92, 60.78) * mm});
            skLineSegment(sketch, "E33.2.0.2", {"start": v(23.62, 60.8) * mm, "end": v(21.45, 62.87) * mm});
            skLineSegment(sketch, "E33.2.0.3", {"start": v(22.92, 60.78) * mm, "end": v(21.47, 62.17) * mm});
            skLineSegment(sketch, "E33.2.0.4", {"start": v(21.55, 58.63) * mm, "end": v(23.62, 60.8) * mm});
            skLineSegment(sketch, "E33.2.0.5", {"start": v(19.38, 60.7) * mm, "end": v(21.55, 58.63) * mm});
            skLineSegment(sketch, "E33.2.0.6", {"start": v(20.09, 60.72) * mm, "end": v(21.53, 59.34) * mm});
            skLineSegment(sketch, "E33.2.0.7", {"start": v(21.45, 62.87) * mm, "end": v(19.38, 60.7) * mm});
            skLineSegment(sketch, "E33.direction1", {"start": v(21.45, 66.49) * mm, "end": v(21.5, 62.56) * mm, "construction": true});
            skLineSegment(sketch, "E34.direction1", {"start": v(-20.72, 68.56) * mm, "end": v(-20.8, 72.8) * mm, "construction": true});
            skLineSegment(sketch, "E35.1.0.0", {"start": v(16.87, 74.47) * mm, "end": v(14.8, 72.3) * mm});
            skLineSegment(sketch, "E35.1.0.1", {"start": v(-1.67, 72.38) * mm, "end": v(-3.11, 73.76) * mm});
            skLineSegment(sketch, "E35.1.0.2", {"start": v(-17.2, 72.3) * mm, "end": v(-15.03, 70.23) * mm});
            skLineSegment(sketch, "E35.1.0.3", {"start": v(-3.05, 70.94) * mm, "end": v(-1.67, 72.38) * mm});
            skLineSegment(sketch, "E35.1.0.4", {"start": v(16.89, 73.76) * mm, "end": v(15.5, 72.32) * mm});
            skLineSegment(sketch, "E35.1.0.5", {"start": v(-11.05, 70.94) * mm, "end": v(-9.67, 72.38) * mm});
            skLineSegment(sketch, "E35.1.0.6", {"start": v(-20.5, 72.32) * mm, "end": v(-19.05, 70.94) * mm});
            skLineSegment(sketch, "E35.1.0.7", {"start": v(-5.2, 72.3) * mm, "end": v(-3.03, 70.23) * mm});
            skLineSegment(sketch, "E35.1.0.8", {"start": v(0.95, 70.94) * mm, "end": v(2.33, 72.38) * mm});
            skLineSegment(sketch, "E35.1.0.9", {"start": v(12.95, 70.94) * mm, "end": v(14.33, 72.38) * mm});
            skLineSegment(sketch, "E35.1.0.10", {"start": v(2.8, 72.3) * mm, "end": v(4.97, 70.23) * mm});
            skLineSegment(sketch, "E35.1.0.11", {"start": v(-13.2, 72.3) * mm, "end": v(-11.03, 70.23) * mm});
            skLineSegment(sketch, "E35.1.0.12", {"start": v(12.87, 74.47) * mm, "end": v(10.8, 72.3) * mm});
            skLineSegment(sketch, "E35.1.0.13", {"start": v(7.04, 72.4) * mm, "end": v(4.87, 74.47) * mm});
            skLineSegment(sketch, "E35.1.0.14", {"start": v(-19.03, 70.23) * mm, "end": v(-16.96, 72.4) * mm});
            skLineSegment(sketch, "E35.1.0.15", {"start": v(10.8, 72.3) * mm, "end": v(12.97, 70.23) * mm});
            skLineSegment(sketch, "E35.1.0.16", {"start": v(8.95, 70.94) * mm, "end": v(10.33, 72.38) * mm});
            skLineSegment(sketch, "E35.1.0.17", {"start": v(-15.03, 70.23) * mm, "end": v(-12.96, 72.4) * mm});
            skLineSegment(sketch, "E35.1.0.18", {"start": v(-1.2, 72.3) * mm, "end": v(0.97, 70.23) * mm});
            skLineSegment(sketch, "E35.1.0.19", {"start": v(-3.03, 70.23) * mm, "end": v(-0.96, 72.4) * mm});
            skLineSegment(sketch, "E35.1.0.20", {"start": v(-19.11, 73.76) * mm, "end": v(-20.5, 72.32) * mm});
            skLineSegment(sketch, "E35.1.0.21", {"start": v(16.97, 70.23) * mm, "end": v(19.04, 72.4) * mm});
            skLineSegment(sketch, "E35.1.0.22", {"start": v(11.5, 72.32) * mm, "end": v(12.95, 70.94) * mm});
            skLineSegment(sketch, "E35.1.0.23", {"start": v(-9.2, 72.3) * mm, "end": v(-7.03, 70.23) * mm});
            skLineSegment(sketch, "E35.1.0.24", {"start": v(0.89, 73.76) * mm, "end": v(-0.5, 72.32) * mm});
            skLineSegment(sketch, "E35.1.0.25", {"start": v(-7.03, 70.23) * mm, "end": v(-4.96, 72.4) * mm});
            skLineSegment(sketch, "E35.1.0.26", {"start": v(-3.13, 74.47) * mm, "end": v(-5.2, 72.3) * mm});
            skLineSegment(sketch, "E35.1.0.27", {"start": v(2.33, 72.38) * mm, "end": v(0.89, 73.76) * mm});
            skLineSegment(sketch, "E35.1.0.28", {"start": v(-15.11, 73.76) * mm, "end": v(-16.5, 72.32) * mm});
            skLineSegment(sketch, "E35.1.0.29", {"start": v(10.33, 72.38) * mm, "end": v(8.89, 73.76) * mm});
            skLineSegment(sketch, "E35.1.0.30", {"start": v(12.97, 70.23) * mm, "end": v(15.04, 72.4) * mm});
            skLineSegment(sketch, "E35.1.0.31", {"start": v(-7.05, 70.94) * mm, "end": v(-5.67, 72.38) * mm});
            skLineSegment(sketch, "E35.1.0.32", {"start": v(-7.13, 74.47) * mm, "end": v(-9.2, 72.3) * mm});
            skLineSegment(sketch, "E35.1.0.33", {"start": v(-11.03, 70.23) * mm, "end": v(-8.96, 72.4) * mm});
            skLineSegment(sketch, "E35.1.0.34", {"start": v(4.97, 70.23) * mm, "end": v(7.04, 72.4) * mm});
            skLineSegment(sketch, "E35.1.0.35", {"start": v(-12.96, 72.4) * mm, "end": v(-15.13, 74.47) * mm});
            skLineSegment(sketch, "E35.1.0.36", {"start": v(-8.96, 72.4) * mm, "end": v(-11.13, 74.47) * mm});
            skLineSegment(sketch, "E35.1.0.37", {"start": v(-0.96, 72.4) * mm, "end": v(-3.13, 74.47) * mm});
            skLineSegment(sketch, "E35.1.0.38", {"start": v(3.04, 72.4) * mm, "end": v(0.87, 74.47) * mm});
            skLineSegment(sketch, "E35.1.0.39", {"start": v(-9.67, 72.38) * mm, "end": v(-11.11, 73.76) * mm});
            skLineSegment(sketch, "E35.1.0.40", {"start": v(-15.05, 70.94) * mm, "end": v(-13.67, 72.38) * mm});
            skLineSegment(sketch, "E35.1.0.41", {"start": v(18.33, 72.38) * mm, "end": v(16.89, 73.76) * mm});
            skLineSegment(sketch, "E35.1.0.42", {"start": v(-12.5, 72.32) * mm, "end": v(-11.05, 70.94) * mm});
            skLineSegment(sketch, "E35.1.0.43", {"start": v(11.04, 72.4) * mm, "end": v(8.87, 74.47) * mm});
            skLineSegment(sketch, "E35.1.0.44", {"start": v(-8.5, 72.32) * mm, "end": v(-7.05, 70.94) * mm});
            skLineSegment(sketch, "E35.1.0.45", {"start": v(8.97, 70.23) * mm, "end": v(11.04, 72.4) * mm});
            skLineSegment(sketch, "E35.1.0.46", {"start": v(-0.5, 72.32) * mm, "end": v(0.95, 70.94) * mm});
            skLineSegment(sketch, "E35.1.0.47", {"start": v(-11.11, 73.76) * mm, "end": v(-12.5, 72.32) * mm});
            skLineSegment(sketch, "E35.1.0.48", {"start": v(14.8, 72.3) * mm, "end": v(16.97, 70.23) * mm});
            skLineSegment(sketch, "E35.1.0.49", {"start": v(20.97, 70.23) * mm, "end": v(23.04, 72.4) * mm});
            skLineSegment(sketch, "E35.1.0.50", {"start": v(16.95, 70.94) * mm, "end": v(18.33, 72.38) * mm});
            skLineSegment(sketch, "E35.1.0.51", {"start": v(-15.13, 74.47) * mm, "end": v(-17.2, 72.3) * mm});
            skLineSegment(sketch, "E35.1.0.52", {"start": v(-5.67, 72.38) * mm, "end": v(-7.11, 73.76) * mm});
            skLineSegment(sketch, "E35.1.0.53", {"start": v(-3.11, 73.76) * mm, "end": v(-4.5, 72.32) * mm});
            skLineSegment(sketch, "E35.1.0.54", {"start": v(-17.67, 72.38) * mm, "end": v(-19.11, 73.76) * mm});
            skLineSegment(sketch, "E35.1.0.55", {"start": v(15.5, 72.32) * mm, "end": v(16.95, 70.94) * mm});
            skLineSegment(sketch, "E35.1.0.56", {"start": v(20.95, 70.94) * mm, "end": v(22.33, 72.38) * mm});
            skLineSegment(sketch, "E35.1.0.57", {"start": v(4.89, 73.76) * mm, "end": v(3.5, 72.32) * mm});
            skLineSegment(sketch, "E35.1.0.58", {"start": v(6.33, 72.38) * mm, "end": v(4.89, 73.76) * mm});
            skLineSegment(sketch, "E35.1.0.59", {"start": v(-16.5, 72.32) * mm, "end": v(-15.05, 70.94) * mm});
            skLineSegment(sketch, "E35.1.0.60", {"start": v(-19.05, 70.94) * mm, "end": v(-17.67, 72.38) * mm});
            skLineSegment(sketch, "E35.1.0.61", {"start": v(7.5, 72.32) * mm, "end": v(8.95, 70.94) * mm});
            skLineSegment(sketch, "E35.1.0.62", {"start": v(-4.96, 72.4) * mm, "end": v(-7.13, 74.47) * mm});
            skLineSegment(sketch, "E35.1.0.63", {"start": v(8.89, 73.76) * mm, "end": v(7.5, 72.32) * mm});
            skLineSegment(sketch, "E35.1.0.64", {"start": v(20.89, 73.76) * mm, "end": v(19.5, 72.32) * mm});
            skLineSegment(sketch, "E35.1.0.65", {"start": v(15.04, 72.4) * mm, "end": v(12.87, 74.47) * mm});
            skLineSegment(sketch, "E35.1.0.66", {"start": v(-21.2, 72.3) * mm, "end": v(-19.03, 70.23) * mm});
            skLineSegment(sketch, "E35.1.0.67", {"start": v(-19.13, 74.47) * mm, "end": v(-21.2, 72.3) * mm});
            skLineSegment(sketch, "E35.1.0.68", {"start": v(0.87, 74.47) * mm, "end": v(-1.2, 72.3) * mm});
            skLineSegment(sketch, "E35.1.0.69", {"start": v(-7.11, 73.76) * mm, "end": v(-8.5, 72.32) * mm});
            skLineSegment(sketch, "E35.1.0.70", {"start": v(3.5, 72.32) * mm, "end": v(4.95, 70.94) * mm});
            skLineSegment(sketch, "E35.1.0.71", {"start": v(8.87, 74.47) * mm, "end": v(6.8, 72.3) * mm});
            skLineSegment(sketch, "E35.1.0.72", {"start": v(14.33, 72.38) * mm, "end": v(12.89, 73.76) * mm});
            skLineSegment(sketch, "E35.1.0.73", {"start": v(6.8, 72.3) * mm, "end": v(8.97, 70.23) * mm});
            skLineSegment(sketch, "E35.1.0.74", {"start": v(22.33, 72.38) * mm, "end": v(20.89, 73.76) * mm});
            skLineSegment(sketch, "E35.1.0.75", {"start": v(19.5, 72.32) * mm, "end": v(20.95, 70.94) * mm});
            skLineSegment(sketch, "E35.1.0.76", {"start": v(23.04, 72.4) * mm, "end": v(20.87, 74.47) * mm});
            skLineSegment(sketch, "E35.1.0.77", {"start": v(19.04, 72.4) * mm, "end": v(16.87, 74.47) * mm});
            skLineSegment(sketch, "E35.1.0.78", {"start": v(-11.13, 74.47) * mm, "end": v(-13.2, 72.3) * mm});
            skLineSegment(sketch, "E35.1.0.79", {"start": v(-4.5, 72.32) * mm, "end": v(-3.05, 70.94) * mm});
            skLineSegment(sketch, "E35.1.0.80", {"start": v(4.87, 74.47) * mm, "end": v(2.8, 72.3) * mm});
            skLineSegment(sketch, "E35.1.0.81", {"start": v(20.87, 74.47) * mm, "end": v(18.8, 72.3) * mm});
            skLineSegment(sketch, "E35.1.0.82", {"start": v(12.89, 73.76) * mm, "end": v(11.5, 72.32) * mm});
            skLineSegment(sketch, "E35.1.0.83", {"start": v(-17.2, 72.3) * mm, "end": v(-21.2, 72.3) * mm, "construction": true});
            skLineSegment(sketch, "E35.1.0.84", {"start": v(-19.11, 73.76) * mm, "end": v(-19.27, 70.77) * mm, "construction": true});
            skLineSegment(sketch, "E35.1.0.85", {"start": v(-17.2, 72.3) * mm, "end": v(-13.2, 72.3) * mm, "construction": true});
            skLineSegment(sketch, "E35.1.0.86", {"start": v(0.97, 70.23) * mm, "end": v(3.04, 72.4) * mm});
            skLineSegment(sketch, "E35.1.0.87", {"start": v(-16.96, 72.4) * mm, "end": v(-19.13, 74.47) * mm});
            skLineSegment(sketch, "E35.1.0.88", {"start": v(4.95, 70.94) * mm, "end": v(6.33, 72.38) * mm});
            skLineSegment(sketch, "E35.1.0.89", {"start": v(18.8, 72.3) * mm, "end": v(20.97, 70.23) * mm});
            skLineSegment(sketch, "E35.1.0.90", {"start": v(-13.67, 72.38) * mm, "end": v(-15.11, 73.76) * mm});
            skLineSegment(sketch, "E35.direction1", {"start": v(-20.72, 68.56) * mm, "end": v(-21.2, 72.3) * mm, "construction": true});
            skSolve(sketch);
        }
        {
            var Q0;
            {var subQ0=sQuery(id+"F13.wireOp",EDGE,"E20");var subQ6=sQuery(id+"F13.wireOp",EDGE,"E29.1.0.1");var subQ7=makeQuery(id+"F13.imprint","INTERSECT",VERTEX,{"derivedFrom":[subQ0,subQ6]});Q0=makeQuery(id+"F13.imprint","IMPRINT",FACE,{"disambiguationData":[TD([[makeQuery(id+"F13.imprint","IMPRINT",EDGE,{"disambiguationData":[TD([[subQ7,-1.0]])],"derivedFrom":subQ6}),-1.0]])]});}
            var Q1;
            {var subQ0=sQuery(id+"F13.wireOp",EDGE,"E29.1.0.2");var subQ1=sQuery(id+"F13.wireOp",EDGE,"E21");var subQ2=makeQuery(id+"F13.imprint","INTERSECT",VERTEX,{"derivedFrom":[subQ1,subQ0]});Q1=makeQuery(id+"F13.imprint","IMPRINT",FACE,{"disambiguationData":[TD([[makeQuery(id+"F13.imprint","IMPRINT",EDGE,{"disambiguationData":[TD([[subQ2,-1.0]])],"derivedFrom":subQ1}),-1.0]])]});}
            var Q2;
            {var subQ0=sQuery(id+"F13.wireOp",EDGE,"E31.1.0.60");var subQ1=sQuery(id+"F13.wireOp",EDGE,"E31.1.0.40");var subQ2=makeQuery(id+"F13.imprint","INTERSECT",VERTEX,{"derivedFrom":[subQ1,subQ0]});Q2=makeQuery(id+"F13.imprint","IMPRINT",FACE,{"disambiguationData":[TD([[makeQuery(id+"F13.imprint","IMPRINT",EDGE,{"disambiguationData":[TD([[subQ2,-1.0]])],"derivedFrom":subQ1}),-1.0]])]});}
            var Q3;
            {var subQ0=sQuery(id+"F13.wireOp",EDGE,"E31.2.0.60");var subQ1=sQuery(id+"F13.wireOp",EDGE,"E31.2.0.40");var subQ2=makeQuery(id+"F13.imprint","INTERSECT",VERTEX,{"derivedFrom":[subQ1,subQ0]});Q3=makeQuery(id+"F13.imprint","IMPRINT",FACE,{"disambiguationData":[TD([[makeQuery(id+"F13.imprint","IMPRINT",EDGE,{"disambiguationData":[TD([[subQ2,-1.0]])],"derivedFrom":subQ1}),-1.0]])]});}
            extrude(context, id + "F14", {"entities" : qUnion([Q0, Q1, Q2, Q3]), "operationType" : NewBodyOperationType.ADD, "depth" : 0.5 * mm, "offsetDistance" : 25 * mm});
        }
        {
            var Q0;
            {var subQ0=sQuery(id+"F13.wireOp",EDGE,"E31.1.0.32");var subQ1=sQuery(id+"F13.wireOp",EDGE,"E22");var subQ2=makeQuery(id+"F13.imprint","INTERSECT",VERTEX,{"derivedFrom":[subQ1,subQ0]});Q0=makeQuery(id+"F13.imprint","IMPRINT",FACE,{"disambiguationData":[TD([[makeQuery(id+"F13.imprint","IMPRINT",EDGE,{"disambiguationData":[TD([[subQ2,-1.0]])],"derivedFrom":subQ1}),-1.0]])]});}
            var Q1;
            {var subQ0=sQuery(id+"F13.wireOp",EDGE,"E31.2.0.32");var subQ1=sQuery(id+"F13.wireOp",EDGE,"E31.1.0.7");var subQ2=makeQuery(id+"F13.imprint","INTERSECT",VERTEX,{"derivedFrom":[subQ1,subQ0]});Q1=makeQuery(id+"F13.imprint","IMPRINT",FACE,{"disambiguationData":[TD([[makeQuery(id+"F13.imprint","IMPRINT",EDGE,{"disambiguationData":[TD([[subQ2,-1.0]])],"derivedFrom":subQ1}),-1.0]])]});}
            var Q2;
            {var subQ0=sQuery(id+"F13.wireOp",EDGE,"E31.3.0.32");var subQ1=sQuery(id+"F13.wireOp",EDGE,"E31.2.0.7");var subQ2=makeQuery(id+"F13.imprint","INTERSECT",VERTEX,{"derivedFrom":[subQ1,subQ0]});Q2=makeQuery(id+"F13.imprint","IMPRINT",FACE,{"disambiguationData":[TD([[makeQuery(id+"F13.imprint","IMPRINT",EDGE,{"disambiguationData":[TD([[subQ2,-1.0]])],"derivedFrom":subQ1}),-1.0]])]});}
            extrude(context, id + "F15", {"entities" : qUnion([Q0, Q1, Q2]), "operationType" : NewBodyOperationType.ADD, "depth" : 0.5 * mm, "offsetDistance" : 25 * mm});
        }
        {
            var Q0;
            {var subQ0=sQuery(id+"F13.wireOp",EDGE,"E31.1.0.2");var subQ1=sQuery(id+"F13.wireOp",EDGE,"E28.1.0.4");var subQ2=makeQuery(id+"F13.imprint","INTERSECT",VERTEX,{"derivedFrom":[subQ1,subQ0]});Q0=makeQuery(id+"F13.imprint","IMPRINT",FACE,{"disambiguationData":[TD([[makeQuery(id+"F13.imprint","IMPRINT",EDGE,{"disambiguationData":[TD([[subQ2,-1.0]])],"derivedFrom":subQ1}),-1.0]])]});}
            var Q1;
            {var subQ0=sQuery(id+"F13.wireOp",EDGE,"E31.1.0.53");var subQ1=sQuery(id+"F13.wireOp",EDGE,"E31.1.0.13");var subQ2=makeQuery(id+"F13.imprint","INTERSECT",VERTEX,{"derivedFrom":[subQ1,subQ0]});Q1=makeQuery(id+"F13.imprint","IMPRINT",FACE,{"disambiguationData":[TD([[makeQuery(id+"F13.imprint","IMPRINT",EDGE,{"disambiguationData":[TD([[subQ2,-1.0]])],"derivedFrom":subQ1}),-1.0]])]});}
            var Q2;
            {var subQ0=sQuery(id+"F13.wireOp",EDGE,"E31.2.0.53");var subQ1=sQuery(id+"F13.wireOp",EDGE,"E31.2.0.13");var subQ2=makeQuery(id+"F13.imprint","INTERSECT",VERTEX,{"derivedFrom":[subQ1,subQ0]});Q2=makeQuery(id+"F13.imprint","IMPRINT",FACE,{"disambiguationData":[TD([[makeQuery(id+"F13.imprint","IMPRINT",EDGE,{"disambiguationData":[TD([[subQ2,-1.0]])],"derivedFrom":subQ1}),-1.0]])]});}
            var Q3;
            {var subQ0=sQuery(id+"F13.wireOp",EDGE,"E31.1.0.71");var subQ1=sQuery(id+"F13.wireOp",EDGE,"E28.2.0.4");var subQ2=makeQuery(id+"F13.imprint","INTERSECT",VERTEX,{"derivedFrom":[subQ1,subQ0]});Q3=makeQuery(id+"F13.imprint","IMPRINT",FACE,{"disambiguationData":[TD([[makeQuery(id+"F13.imprint","IMPRINT",EDGE,{"disambiguationData":[TD([[subQ2,-1.0]])],"derivedFrom":subQ1}),-1.0]])]});}
            var Q4;
            {var subQ0=sQuery(id+"F13.wireOp",EDGE,"E31.2.0.71");var subQ1=sQuery(id+"F13.wireOp",EDGE,"E31.1.0.48");var subQ2=makeQuery(id+"F13.imprint","INTERSECT",VERTEX,{"derivedFrom":[subQ1,subQ0]});Q4=makeQuery(id+"F13.imprint","IMPRINT",FACE,{"disambiguationData":[TD([[makeQuery(id+"F13.imprint","IMPRINT",EDGE,{"disambiguationData":[TD([[subQ2,-1.0]])],"derivedFrom":subQ1}),-1.0]])]});}
            var Q5;
            {var subQ0=sQuery(id+"F13.wireOp",EDGE,"E31.3.0.71");var subQ1=sQuery(id+"F13.wireOp",EDGE,"E31.2.0.48");var subQ2=makeQuery(id+"F13.imprint","INTERSECT",VERTEX,{"derivedFrom":[subQ1,subQ0]});Q5=makeQuery(id+"F13.imprint","IMPRINT",FACE,{"disambiguationData":[TD([[makeQuery(id+"F13.imprint","IMPRINT",EDGE,{"disambiguationData":[TD([[subQ2,-1.0]])],"derivedFrom":subQ1}),-1.0]])]});}
            var Q6;
            {var subQ0=sQuery(id+"F13.wireOp",EDGE,"E31.3.0.31");var subQ1=sQuery(id+"F13.wireOp",EDGE,"E31.2.0.52");var subQ2=makeQuery(id+"F13.imprint","INTERSECT",VERTEX,{"derivedFrom":[subQ1,subQ0]});Q6=makeQuery(id+"F13.imprint","IMPRINT",FACE,{"disambiguationData":[TD([[makeQuery(id+"F13.imprint","IMPRINT",EDGE,{"disambiguationData":[TD([[subQ2,-1.0]])],"derivedFrom":subQ1}),-1.0]])]});}
            var Q7;
            {var subQ0=sQuery(id+"F13.wireOp",EDGE,"E31.2.0.31");var subQ1=sQuery(id+"F13.wireOp",EDGE,"E31.1.0.52");var subQ2=makeQuery(id+"F13.imprint","INTERSECT",VERTEX,{"derivedFrom":[subQ1,subQ0]});Q7=makeQuery(id+"F13.imprint","IMPRINT",FACE,{"disambiguationData":[TD([[makeQuery(id+"F13.imprint","IMPRINT",EDGE,{"disambiguationData":[TD([[subQ2,-1.0]])],"derivedFrom":subQ1}),-1.0]])]});}
            var Q8;
            {var subQ0=sQuery(id+"F13.wireOp",EDGE,"E31.1.0.31");var subQ1=sQuery(id+"F13.wireOp",EDGE,"E28.3.0.4");var subQ2=makeQuery(id+"F13.imprint","INTERSECT",VERTEX,{"derivedFrom":[subQ1,subQ0]});Q8=makeQuery(id+"F13.imprint","IMPRINT",FACE,{"disambiguationData":[TD([[makeQuery(id+"F13.imprint","IMPRINT",EDGE,{"disambiguationData":[TD([[subQ2,-1.0]])],"derivedFrom":subQ1}),-1.0]])]});}
            extrude(context, id + "F16", {"entities" : qUnion([Q0, Q1, Q2, Q3, Q4, Q5, Q6, Q7, Q8]), "operationType" : NewBodyOperationType.ADD, "depth" : 0.5 * mm, "offsetDistance" : 25 * mm});
        }
        {
            var Q0;
            {var subQ0=sQuery(id+"F13.wireOp",EDGE,"E31.1.0.71");var subQ1=sQuery(id+"F13.wireOp",EDGE,"E28.2.0.4");var subQ2=makeQuery(id+"F13.imprint","INTERSECT",VERTEX,{"derivedFrom":[subQ1,subQ0]});Q0=makeQuery(id+"F13.imprint","IMPRINT",FACE,{"disambiguationData":[TD([[makeQuery(id+"F13.imprint","IMPRINT",EDGE,{"disambiguationData":[TD([[subQ2,-1.0]])],"derivedFrom":subQ1}),-1.0]])]});}
            var Q1;
            {var subQ0=sQuery(id+"F13.wireOp",EDGE,"E31.2.0.71");var subQ1=sQuery(id+"F13.wireOp",EDGE,"E31.1.0.48");var subQ2=makeQuery(id+"F13.imprint","INTERSECT",VERTEX,{"derivedFrom":[subQ1,subQ0]});Q1=makeQuery(id+"F13.imprint","IMPRINT",FACE,{"disambiguationData":[TD([[makeQuery(id+"F13.imprint","IMPRINT",EDGE,{"disambiguationData":[TD([[subQ2,-1.0]])],"derivedFrom":subQ1}),-1.0]])]});}
            var Q2;
            {var subQ0=sQuery(id+"F13.wireOp",EDGE,"E31.3.0.71");var subQ1=sQuery(id+"F13.wireOp",EDGE,"E31.2.0.48");var subQ2=makeQuery(id+"F13.imprint","INTERSECT",VERTEX,{"derivedFrom":[subQ1,subQ0]});Q2=makeQuery(id+"F13.imprint","IMPRINT",FACE,{"disambiguationData":[TD([[makeQuery(id+"F13.imprint","IMPRINT",EDGE,{"disambiguationData":[TD([[subQ2,-1.0]])],"derivedFrom":subQ1}),-1.0]])]});}
            var Q3;
            {var subQ0=sQuery(id+"F13.wireOp",EDGE,"E31.3.0.31");var subQ1=sQuery(id+"F13.wireOp",EDGE,"E31.2.0.52");var subQ2=makeQuery(id+"F13.imprint","INTERSECT",VERTEX,{"derivedFrom":[subQ1,subQ0]});Q3=makeQuery(id+"F13.imprint","IMPRINT",FACE,{"disambiguationData":[TD([[makeQuery(id+"F13.imprint","IMPRINT",EDGE,{"disambiguationData":[TD([[subQ2,-1.0]])],"derivedFrom":subQ1}),-1.0]])]});}
            var Q4;
            {var subQ0=sQuery(id+"F13.wireOp",EDGE,"E31.2.0.31");var subQ1=sQuery(id+"F13.wireOp",EDGE,"E31.1.0.52");var subQ2=makeQuery(id+"F13.imprint","INTERSECT",VERTEX,{"derivedFrom":[subQ1,subQ0]});Q4=makeQuery(id+"F13.imprint","IMPRINT",FACE,{"disambiguationData":[TD([[makeQuery(id+"F13.imprint","IMPRINT",EDGE,{"disambiguationData":[TD([[subQ2,-1.0]])],"derivedFrom":subQ1}),-1.0]])]});}
            var Q5;
            {var subQ0=sQuery(id+"F13.wireOp",EDGE,"E31.1.0.31");var subQ1=sQuery(id+"F13.wireOp",EDGE,"E28.3.0.4");var subQ2=makeQuery(id+"F13.imprint","INTERSECT",VERTEX,{"derivedFrom":[subQ1,subQ0]});Q5=makeQuery(id+"F13.imprint","IMPRINT",FACE,{"disambiguationData":[TD([[makeQuery(id+"F13.imprint","IMPRINT",EDGE,{"disambiguationData":[TD([[subQ2,-1.0]])],"derivedFrom":subQ1}),-1.0]])]});}
            extrude(context, id + "F17", {"entities" : qUnion([Q0, Q1, Q2, Q3, Q4, Q5]), "operationType" : NewBodyOperationType.ADD, "depth" : 0.5 * mm, "offsetDistance" : 25 * mm});
        }
        {
            var Q0;
            {var subQ0=sQuery(id+"F13.wireOp",EDGE,"E31.1.0.25");var subQ1=sQuery(id+"F13.wireOp",EDGE,"E28.4.0.4");var subQ2=makeQuery(id+"F13.imprint","INTERSECT",VERTEX,{"derivedFrom":[subQ1,subQ0]});Q0=makeQuery(id+"F13.imprint","IMPRINT",FACE,{"disambiguationData":[TD([[makeQuery(id+"F13.imprint","IMPRINT",EDGE,{"disambiguationData":[TD([[subQ2,-1.0]])],"derivedFrom":subQ1}),-1.0]])]});}
            var Q1;
            {var subQ0=sQuery(id+"F13.wireOp",EDGE,"E31.2.0.25");var subQ1=sQuery(id+"F13.wireOp",EDGE,"E31.1.0.12");var subQ2=makeQuery(id+"F13.imprint","INTERSECT",VERTEX,{"derivedFrom":[subQ1,subQ0]});Q1=makeQuery(id+"F13.imprint","IMPRINT",FACE,{"disambiguationData":[TD([[makeQuery(id+"F13.imprint","IMPRINT",EDGE,{"disambiguationData":[TD([[subQ2,-1.0]])],"derivedFrom":subQ1}),-1.0]])]});}
            var Q2;
            {var subQ0=sQuery(id+"F13.wireOp",EDGE,"E31.3.0.25");var subQ1=sQuery(id+"F13.wireOp",EDGE,"E31.2.0.12");var subQ2=makeQuery(id+"F13.imprint","INTERSECT",VERTEX,{"derivedFrom":[subQ1,subQ0]});Q2=makeQuery(id+"F13.imprint","IMPRINT",FACE,{"disambiguationData":[TD([[makeQuery(id+"F13.imprint","IMPRINT",EDGE,{"disambiguationData":[TD([[subQ2,-1.0]])],"derivedFrom":subQ1}),-1.0]])]});}
            var Q3;
            {var subQ0=sQuery(id+"F13.wireOp",EDGE,"E31.3.0.43");var subQ1=sQuery(id+"F13.wireOp",EDGE,"E31.2.0.44");var subQ2=makeQuery(id+"F13.imprint","INTERSECT",VERTEX,{"derivedFrom":[subQ1,subQ0]});Q3=makeQuery(id+"F13.imprint","IMPRINT",FACE,{"disambiguationData":[TD([[makeQuery(id+"F13.imprint","IMPRINT",EDGE,{"disambiguationData":[TD([[subQ2,-1.0]])],"derivedFrom":subQ1}),-1.0]])]});}
            var Q4;
            {var subQ0=sQuery(id+"F13.wireOp",EDGE,"E31.2.0.43");var subQ1=sQuery(id+"F13.wireOp",EDGE,"E31.1.0.44");var subQ2=makeQuery(id+"F13.imprint","INTERSECT",VERTEX,{"derivedFrom":[subQ1,subQ0]});Q4=makeQuery(id+"F13.imprint","IMPRINT",FACE,{"disambiguationData":[TD([[makeQuery(id+"F13.imprint","IMPRINT",EDGE,{"disambiguationData":[TD([[subQ2,-1.0]])],"derivedFrom":subQ1}),-1.0]])]});}
            var Q5;
            {var subQ0=sQuery(id+"F13.wireOp",EDGE,"E31.1.0.43");var subQ1=sQuery(id+"F13.wireOp",EDGE,"E28.5.0.4");var subQ2=makeQuery(id+"F13.imprint","INTERSECT",VERTEX,{"derivedFrom":[subQ1,subQ0]});Q5=makeQuery(id+"F13.imprint","IMPRINT",FACE,{"disambiguationData":[TD([[makeQuery(id+"F13.imprint","IMPRINT",EDGE,{"disambiguationData":[TD([[subQ2,-1.0]])],"derivedFrom":subQ1}),-1.0]])]});}
            var Q6;
            {var subQ0=sQuery(id+"F13.wireOp",EDGE,"E31.1.0.46");var subQ1=sQuery(id+"F13.wireOp",EDGE,"E28.6.0.4");var subQ2=makeQuery(id+"F13.imprint","INTERSECT",VERTEX,{"derivedFrom":[subQ1,subQ0]});Q6=makeQuery(id+"F13.imprint","IMPRINT",FACE,{"disambiguationData":[TD([[makeQuery(id+"F13.imprint","IMPRINT",EDGE,{"disambiguationData":[TD([[subQ2,-1.0]])],"derivedFrom":subQ1}),-1.0]])]});}
            var Q7;
            {var subQ0=sQuery(id+"F13.wireOp",EDGE,"E31.1.0.41");var subQ1=sQuery(id+"F13.wireOp",EDGE,"E31.1.0.27");var subQ2=makeQuery(id+"F13.imprint","INTERSECT",VERTEX,{"derivedFrom":[subQ1,subQ0]});Q7=makeQuery(id+"F13.imprint","IMPRINT",FACE,{"disambiguationData":[TD([[makeQuery(id+"F13.imprint","IMPRINT",EDGE,{"disambiguationData":[TD([[subQ2,-1.0]])],"derivedFrom":subQ1}),-1.0]])]});}
            var Q8;
            {var subQ0=sQuery(id+"F13.wireOp",EDGE,"E31.2.0.41");var subQ1=sQuery(id+"F13.wireOp",EDGE,"E31.2.0.27");var subQ2=makeQuery(id+"F13.imprint","INTERSECT",VERTEX,{"derivedFrom":[subQ1,subQ0]});Q8=makeQuery(id+"F13.imprint","IMPRINT",FACE,{"disambiguationData":[TD([[makeQuery(id+"F13.imprint","IMPRINT",EDGE,{"disambiguationData":[TD([[subQ2,-1.0]])],"derivedFrom":subQ1}),-1.0]])]});}
            extrude(context, id + "F18", {"entities" : qUnion([Q0, Q1, Q2, Q3, Q4, Q5, Q6, Q7, Q8]), "operationType" : NewBodyOperationType.ADD, "depth" : 0.5 * mm, "offsetDistance" : 25 * mm});
        }
        {
            var Q0;
            {var subQ0=sQuery(id+"F13.wireOp",EDGE,"E31.1.0.78");var subQ1=sQuery(id+"F13.wireOp",EDGE,"E28.7.0.4");var subQ2=makeQuery(id+"F13.imprint","INTERSECT",VERTEX,{"derivedFrom":[subQ1,subQ0]});Q0=makeQuery(id+"F13.imprint","IMPRINT",FACE,{"disambiguationData":[TD([[makeQuery(id+"F13.imprint","IMPRINT",EDGE,{"disambiguationData":[TD([[subQ2,-1.0]])],"derivedFrom":subQ1}),-1.0]])]});}
            var Q1;
            {var subQ0=sQuery(id+"F13.wireOp",EDGE,"E31.2.0.78");var subQ1=sQuery(id+"F13.wireOp",EDGE,"E31.1.0.5");var subQ2=makeQuery(id+"F13.imprint","INTERSECT",VERTEX,{"derivedFrom":[subQ1,subQ0]});Q1=makeQuery(id+"F13.imprint","IMPRINT",FACE,{"disambiguationData":[TD([[makeQuery(id+"F13.imprint","IMPRINT",EDGE,{"disambiguationData":[TD([[subQ2,-1.0]])],"derivedFrom":subQ1}),-1.0]])]});}
            var Q2;
            {var subQ0=sQuery(id+"F13.wireOp",EDGE,"E31.3.0.78");var subQ1=sQuery(id+"F13.wireOp",EDGE,"E31.2.0.5");var subQ2=makeQuery(id+"F13.imprint","INTERSECT",VERTEX,{"derivedFrom":[subQ1,subQ0]});Q2=makeQuery(id+"F13.imprint","IMPRINT",FACE,{"disambiguationData":[TD([[makeQuery(id+"F13.imprint","IMPRINT",EDGE,{"disambiguationData":[TD([[subQ2,-1.0]])],"derivedFrom":subQ1}),-1.0]])]});}
            var Q3;
            {var subQ1=sQuery(id+"F13.wireOp",EDGE,"E31.2.0.42");var subQ6=sQuery(id+"F13.wireOp",EDGE,"E31.1.0.63");var subQ7=makeQuery(id+"F13.imprint","INTERSECT",VERTEX,{"derivedFrom":[subQ6,subQ1]});Q3=makeQuery(id+"F13.imprint","IMPRINT",FACE,{"disambiguationData":[TD([[makeQuery(id+"F13.imprint","IMPRINT",EDGE,{"disambiguationData":[TD([[subQ7,-1.0]])],"derivedFrom":subQ6}),-1.0]])]});}
            var Q4;
            {var subQ0=sQuery(id+"F13.wireOp",EDGE,"E31.1.0.42");var subQ1=sQuery(id+"F13.wireOp",EDGE,"E28.8.0.4");var subQ2=makeQuery(id+"F13.imprint","INTERSECT",VERTEX,{"derivedFrom":[subQ1,subQ0]});Q4=makeQuery(id+"F13.imprint","IMPRINT",FACE,{"disambiguationData":[TD([[makeQuery(id+"F13.imprint","IMPRINT",EDGE,{"disambiguationData":[TD([[subQ2,1.0]])],"derivedFrom":subQ0}),-1.0]])]});}
            extrude(context, id + "F19", {"entities" : qUnion([Q0, Q1, Q2, Q3, Q4]), "operationType" : NewBodyOperationType.ADD, "depth" : 0.5 * mm, "offsetDistance" : 25 * mm});
        }
        {
            var Q0;
            {var subQ0=sQuery(id+"F13.wireOp",EDGE,"E31.3.0.42");var subQ1=sQuery(id+"F13.wireOp",EDGE,"E31.2.0.63");var subQ2=makeQuery(id+"F13.imprint","INTERSECT",VERTEX,{"derivedFrom":[subQ1,subQ0]});Q0=makeQuery(id+"F13.imprint","IMPRINT",FACE,{"disambiguationData":[TD([[makeQuery(id+"F13.imprint","IMPRINT",EDGE,{"disambiguationData":[TD([[subQ2,-1.0]])],"derivedFrom":subQ1}),-1.0]])]});}
            extrude(context, id + "F20", {"entities" : qUnion([Q0]), "operationType" : NewBodyOperationType.ADD, "depth" : 0.5 * mm, "offsetDistance" : 25 * mm});
        }
        {
            var Q0;
            {var subQ0=sQuery(id+"F13.wireOp",EDGE,"E31.1.0.34");var subQ1=sQuery(id+"F13.wireOp",EDGE,"E29.1.0.7");var subQ2=makeQuery(id+"F13.imprint","INTERSECT",VERTEX,{"derivedFrom":[subQ1,subQ0]});Q0=makeQuery(id+"F13.imprint","IMPRINT",FACE,{"disambiguationData":[TD([[makeQuery(id+"F13.imprint","IMPRINT",EDGE,{"disambiguationData":[TD([[subQ2,1.0]])],"derivedFrom":subQ1}),-1.0]])]});}
            var Q1;
            {var subQ0=sQuery(id+"F13.wireOp",EDGE,"E31.2.0.34");var subQ1=sQuery(id+"F13.wireOp",EDGE,"E31.1.0.18");var subQ2=makeQuery(id+"F13.imprint","INTERSECT",VERTEX,{"derivedFrom":[subQ1,subQ0]});Q1=makeQuery(id+"F13.imprint","IMPRINT",FACE,{"disambiguationData":[TD([[makeQuery(id+"F13.imprint","IMPRINT",EDGE,{"disambiguationData":[TD([[subQ2,1.0]])],"derivedFrom":subQ1}),-1.0]])]});}
            extrude(context, id + "F21", {"entities" : qUnion([Q0, Q1]), "operationType" : NewBodyOperationType.ADD, "depth" : 0.5 * mm, "offsetDistance" : 25 * mm});
        }
        {
            var Q0;
            {var subQ1=sQuery(id+"F13.wireOp",EDGE,"E23");var subQ7=sQuery(id+"F13.wireOp",EDGE,"E28.1.0.0");var subQ10=makeQuery(id+"F13.imprint","INTERSECT",VERTEX,{"derivedFrom":[subQ1,subQ7]});Q0=makeQuery(id+"F13.imprint","IMPRINT",FACE,{"disambiguationData":[TD([[makeQuery(id+"F13.imprint","IMPRINT",EDGE,{"disambiguationData":[TD([[subQ10,-1.0]])],"derivedFrom":subQ1}),-1.0]])]});}
            var Q1;
            {var subQ1=sQuery(id+"F13.wireOp",EDGE,"E28.1.0.3");var subQ7=sQuery(id+"F13.wireOp",EDGE,"E28.2.0.0");var subQ10=makeQuery(id+"F13.imprint","INTERSECT",VERTEX,{"derivedFrom":[subQ1,subQ7]});Q1=makeQuery(id+"F13.imprint","IMPRINT",FACE,{"disambiguationData":[TD([[makeQuery(id+"F13.imprint","IMPRINT",EDGE,{"disambiguationData":[TD([[subQ10,-1.0]])],"derivedFrom":subQ1}),-1.0]])]});}
            var Q2;
            {var subQ1=sQuery(id+"F13.wireOp",EDGE,"E28.3.0.0");var subQ8=sQuery(id+"F13.wireOp",EDGE,"E28.2.0.3");var subQ9=makeQuery(id+"F13.imprint","INTERSECT",VERTEX,{"derivedFrom":[subQ8,subQ1]});Q2=makeQuery(id+"F13.imprint","IMPRINT",FACE,{"disambiguationData":[TD([[makeQuery(id+"F13.imprint","IMPRINT",EDGE,{"disambiguationData":[TD([[subQ9,-1.0]])],"derivedFrom":subQ8}),-1.0]])]});}
            var Q3;
            {var subQ1=sQuery(id+"F13.wireOp",EDGE,"E28.4.0.0");var subQ6=sQuery(id+"F13.wireOp",EDGE,"E28.3.0.3");var subQ7=makeQuery(id+"F13.imprint","INTERSECT",VERTEX,{"derivedFrom":[subQ6,subQ1]});Q3=makeQuery(id+"F13.imprint","IMPRINT",FACE,{"disambiguationData":[TD([[makeQuery(id+"F13.imprint","IMPRINT",EDGE,{"disambiguationData":[TD([[subQ7,-1.0]])],"derivedFrom":subQ6}),-1.0]])]});}
            var Q4;
            {var subQ1=sQuery(id+"F13.wireOp",EDGE,"E28.4.0.3");var subQ7=sQuery(id+"F13.wireOp",EDGE,"E28.5.0.0");var subQ10=makeQuery(id+"F13.imprint","INTERSECT",VERTEX,{"derivedFrom":[subQ1,subQ7]});Q4=makeQuery(id+"F13.imprint","IMPRINT",FACE,{"disambiguationData":[TD([[makeQuery(id+"F13.imprint","IMPRINT",EDGE,{"disambiguationData":[TD([[subQ10,-1.0]])],"derivedFrom":subQ1}),-1.0]])]});}
            var Q5;
            {var subQ1=sQuery(id+"F13.wireOp",EDGE,"E28.6.0.0");var subQ8=sQuery(id+"F13.wireOp",EDGE,"E28.5.0.3");var subQ10=makeQuery(id+"F13.imprint","INTERSECT",VERTEX,{"derivedFrom":[subQ8,subQ1]});Q5=makeQuery(id+"F13.imprint","IMPRINT",FACE,{"disambiguationData":[TD([[makeQuery(id+"F13.imprint","IMPRINT",EDGE,{"disambiguationData":[TD([[subQ10,-1.0]])],"derivedFrom":subQ8}),-1.0]])]});}
            var Q6;
            {var subQ0=sQuery(id+"F13.wireOp",EDGE,"E28.7.0.0");var subQ1=sQuery(id+"F13.wireOp",EDGE,"E28.6.0.3");var subQ2=makeQuery(id+"F13.imprint","INTERSECT",VERTEX,{"derivedFrom":[subQ1,subQ0]});Q6=makeQuery(id+"F13.imprint","IMPRINT",FACE,{"disambiguationData":[TD([[makeQuery(id+"F13.imprint","IMPRINT",EDGE,{"disambiguationData":[TD([[subQ2,-1.0]])],"derivedFrom":subQ1}),-1.0]])]});}
            var Q7;
            {var subQ1=sQuery(id+"F13.wireOp",EDGE,"E28.7.0.3");var subQ10=sQuery(id+"F13.wireOp",EDGE,"E28.8.0.0");var subQ11=makeQuery(id+"F13.imprint","INTERSECT",VERTEX,{"derivedFrom":[subQ1,subQ10]});Q7=makeQuery(id+"F13.imprint","IMPRINT",FACE,{"disambiguationData":[TD([[makeQuery(id+"F13.imprint","IMPRINT",EDGE,{"disambiguationData":[TD([[subQ11,-1.0]])],"derivedFrom":subQ1}),-1.0]])]});}
            extrude(context, id + "F22", {"entities" : qUnion([Q0, Q1, Q2, Q3, Q4, Q5, Q6, Q7]), "operationType" : NewBodyOperationType.ADD, "depth" : 0.5 * mm, "offsetDistance" : 25 * mm});
        }
    });
